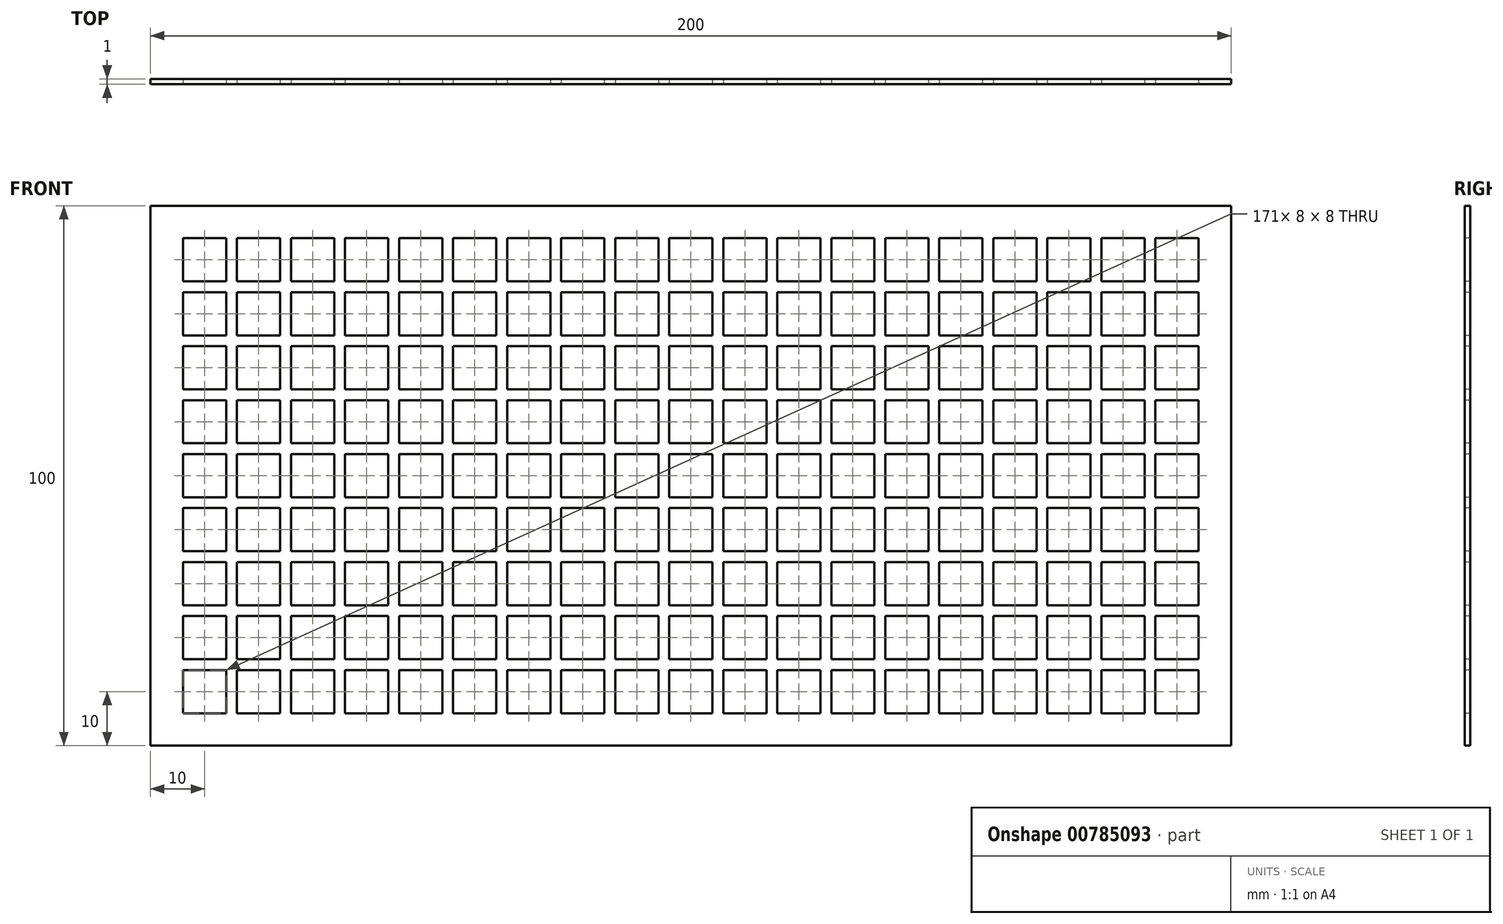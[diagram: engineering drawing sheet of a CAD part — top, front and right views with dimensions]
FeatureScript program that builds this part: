
annotation { "Feature Type Name" : "Feature", "Feature Type Description" : "" }
export const myFeature = defineFeature(function(context is Context, id is Id, definition is map)
    precondition{}
    {
        {
            var Q0;
            Q0=qCreatedBy(makeId("Front.planeOp"),FACE);
            var sketch = newSketch(context, id + "F0", { "sketchPlane" : qUnion([Q0])});
            skLineSegment(sketch, "E0.bottom", {"start": v(0, 0) * mm, "end": v(200, 0) * mm});
            skLineSegment(sketch, "E0.top", {"start": v(0, 100) * mm, "end": v(200, 100) * mm});
            skLineSegment(sketch, "E0.left", {"start": v(0, 0) * mm, "end": v(0, 100) * mm});
            skLineSegment(sketch, "E0.right", {"start": v(200, 0) * mm, "end": v(200, 100) * mm});
            skSolve(sketch);
        }
        {
            var Q0;
            Q0=makeQuery(id+"F0.imprint","IMPRINT",FACE,{"disambiguationData":[TD([[makeQuery(id+"F0.imprint","IMPRINT",EDGE,{"derivedFrom":sQuery(id+"F0.wireOp",EDGE,"E0.bottom")}),1.0]])]});
            extrude(context, id + "F1", {"entities" : qUnion([Q0]), "depth" : 1 * mm, "offsetDistance" : 25 * mm});
        }
        {
            var Q0;
            Q0=makeQuery(id+"F1.opExtrude","CAP_FACE",FACE,{"disambiguationData":[OSD([sQuery(id+"F0.wireOp",EDGE,"E0.bottom"),sQuery(id+"F0.wireOp",EDGE,"E0.top"),sQuery(id+"F0.wireOp",EDGE,"E0.left"),sQuery(id+"F0.wireOp",EDGE,"E0.right")])],"isStart":false});
            var sketch = newSketch(context, id + "F2", { "sketchPlane" : qUnion([Q0])});
            skLineSegment(sketch, "E1.bottom", {"start": v(6, 94) * mm, "end": v(14, 94) * mm});
            skLineSegment(sketch, "E1.top", {"start": v(6, 86) * mm, "end": v(14, 86) * mm});
            skLineSegment(sketch, "E1.left", {"start": v(6, 94) * mm, "end": v(6, 86) * mm});
            skLineSegment(sketch, "E1.right", {"start": v(14, 94) * mm, "end": v(14, 86) * mm});
            skLineSegment(sketch, "E2.0.1.0", {"start": v(14, 84) * mm, "end": v(14, 76) * mm});
            skLineSegment(sketch, "E2.0.1.1", {"start": v(6, 84) * mm, "end": v(6, 76) * mm});
            skLineSegment(sketch, "E2.0.1.2", {"start": v(6, 76) * mm, "end": v(14, 76) * mm});
            skLineSegment(sketch, "E2.0.1.3", {"start": v(6, 84) * mm, "end": v(14, 84) * mm});
            skLineSegment(sketch, "E2.0.2.0", {"start": v(14, 74) * mm, "end": v(14, 66) * mm});
            skLineSegment(sketch, "E2.0.2.1", {"start": v(6, 74) * mm, "end": v(6, 66) * mm});
            skLineSegment(sketch, "E2.0.2.2", {"start": v(6, 66) * mm, "end": v(14, 66) * mm});
            skLineSegment(sketch, "E2.0.2.3", {"start": v(6, 74) * mm, "end": v(14, 74) * mm});
            skLineSegment(sketch, "E2.0.3.0", {"start": v(14, 64) * mm, "end": v(14, 56) * mm});
            skLineSegment(sketch, "E2.0.3.1", {"start": v(6, 64) * mm, "end": v(6, 56) * mm});
            skLineSegment(sketch, "E2.0.3.2", {"start": v(6, 56) * mm, "end": v(14, 56) * mm});
            skLineSegment(sketch, "E2.0.3.3", {"start": v(6, 64) * mm, "end": v(14, 64) * mm});
            skLineSegment(sketch, "E2.0.4.0", {"start": v(14, 54) * mm, "end": v(14, 46) * mm});
            skLineSegment(sketch, "E2.0.4.1", {"start": v(6, 54) * mm, "end": v(6, 46) * mm});
            skLineSegment(sketch, "E2.0.4.2", {"start": v(6, 46) * mm, "end": v(14, 46) * mm});
            skLineSegment(sketch, "E2.0.4.3", {"start": v(6, 54) * mm, "end": v(14, 54) * mm});
            skLineSegment(sketch, "E2.0.5.0", {"start": v(14, 44) * mm, "end": v(14, 36) * mm});
            skLineSegment(sketch, "E2.0.5.1", {"start": v(6, 44) * mm, "end": v(6, 36) * mm});
            skLineSegment(sketch, "E2.0.5.2", {"start": v(6, 36) * mm, "end": v(14, 36) * mm});
            skLineSegment(sketch, "E2.0.5.3", {"start": v(6, 44) * mm, "end": v(14, 44) * mm});
            skLineSegment(sketch, "E2.0.6.0", {"start": v(14, 34) * mm, "end": v(14, 26) * mm});
            skLineSegment(sketch, "E2.0.6.1", {"start": v(6, 34) * mm, "end": v(6, 26) * mm});
            skLineSegment(sketch, "E2.0.6.2", {"start": v(6, 26) * mm, "end": v(14, 26) * mm});
            skLineSegment(sketch, "E2.0.6.3", {"start": v(6, 34) * mm, "end": v(14, 34) * mm});
            skLineSegment(sketch, "E2.0.7.0", {"start": v(14, 24) * mm, "end": v(14, 16) * mm});
            skLineSegment(sketch, "E2.0.7.1", {"start": v(6, 24) * mm, "end": v(6, 16) * mm});
            skLineSegment(sketch, "E2.0.7.2", {"start": v(6, 16) * mm, "end": v(14, 16) * mm});
            skLineSegment(sketch, "E2.0.7.3", {"start": v(6, 24) * mm, "end": v(14, 24) * mm});
            skLineSegment(sketch, "E2.0.8.0", {"start": v(14, 14) * mm, "end": v(14, 6) * mm});
            skLineSegment(sketch, "E2.0.8.1", {"start": v(6, 14) * mm, "end": v(6, 6) * mm});
            skLineSegment(sketch, "E2.0.8.2", {"start": v(6, 6) * mm, "end": v(14, 6) * mm});
            skLineSegment(sketch, "E2.0.8.3", {"start": v(6, 14) * mm, "end": v(14, 14) * mm});
            skLineSegment(sketch, "E2.1.0.0", {"start": v(24, 94) * mm, "end": v(24, 86) * mm});
            skLineSegment(sketch, "E2.1.0.1", {"start": v(16, 94) * mm, "end": v(16, 86) * mm});
            skLineSegment(sketch, "E2.1.0.2", {"start": v(16, 86) * mm, "end": v(24, 86) * mm});
            skLineSegment(sketch, "E2.1.0.3", {"start": v(16, 94) * mm, "end": v(24, 94) * mm});
            skLineSegment(sketch, "E2.1.1.0", {"start": v(24, 84) * mm, "end": v(24, 76) * mm});
            skLineSegment(sketch, "E2.1.1.1", {"start": v(16, 84) * mm, "end": v(16, 76) * mm});
            skLineSegment(sketch, "E2.1.1.2", {"start": v(16, 76) * mm, "end": v(24, 76) * mm});
            skLineSegment(sketch, "E2.1.1.3", {"start": v(16, 84) * mm, "end": v(24, 84) * mm});
            skLineSegment(sketch, "E2.1.2.0", {"start": v(24, 74) * mm, "end": v(24, 66) * mm});
            skLineSegment(sketch, "E2.1.2.1", {"start": v(16, 74) * mm, "end": v(16, 66) * mm});
            skLineSegment(sketch, "E2.1.2.2", {"start": v(16, 66) * mm, "end": v(24, 66) * mm});
            skLineSegment(sketch, "E2.1.2.3", {"start": v(16, 74) * mm, "end": v(24, 74) * mm});
            skLineSegment(sketch, "E2.1.3.0", {"start": v(24, 64) * mm, "end": v(24, 56) * mm});
            skLineSegment(sketch, "E2.1.3.1", {"start": v(16, 64) * mm, "end": v(16, 56) * mm});
            skLineSegment(sketch, "E2.1.3.2", {"start": v(16, 56) * mm, "end": v(24, 56) * mm});
            skLineSegment(sketch, "E2.1.3.3", {"start": v(16, 64) * mm, "end": v(24, 64) * mm});
            skLineSegment(sketch, "E2.1.4.0", {"start": v(24, 54) * mm, "end": v(24, 46) * mm});
            skLineSegment(sketch, "E2.1.4.1", {"start": v(16, 54) * mm, "end": v(16, 46) * mm});
            skLineSegment(sketch, "E2.1.4.2", {"start": v(16, 46) * mm, "end": v(24, 46) * mm});
            skLineSegment(sketch, "E2.1.4.3", {"start": v(16, 54) * mm, "end": v(24, 54) * mm});
            skLineSegment(sketch, "E2.1.5.0", {"start": v(24, 44) * mm, "end": v(24, 36) * mm});
            skLineSegment(sketch, "E2.1.5.1", {"start": v(16, 44) * mm, "end": v(16, 36) * mm});
            skLineSegment(sketch, "E2.1.5.2", {"start": v(16, 36) * mm, "end": v(24, 36) * mm});
            skLineSegment(sketch, "E2.1.5.3", {"start": v(16, 44) * mm, "end": v(24, 44) * mm});
            skLineSegment(sketch, "E2.1.6.0", {"start": v(24, 34) * mm, "end": v(24, 26) * mm});
            skLineSegment(sketch, "E2.1.6.1", {"start": v(16, 34) * mm, "end": v(16, 26) * mm});
            skLineSegment(sketch, "E2.1.6.2", {"start": v(16, 26) * mm, "end": v(24, 26) * mm});
            skLineSegment(sketch, "E2.1.6.3", {"start": v(16, 34) * mm, "end": v(24, 34) * mm});
            skLineSegment(sketch, "E2.1.7.0", {"start": v(24, 24) * mm, "end": v(24, 16) * mm});
            skLineSegment(sketch, "E2.1.7.1", {"start": v(16, 24) * mm, "end": v(16, 16) * mm});
            skLineSegment(sketch, "E2.1.7.2", {"start": v(16, 16) * mm, "end": v(24, 16) * mm});
            skLineSegment(sketch, "E2.1.7.3", {"start": v(16, 24) * mm, "end": v(24, 24) * mm});
            skLineSegment(sketch, "E2.1.8.0", {"start": v(24, 14) * mm, "end": v(24, 6) * mm});
            skLineSegment(sketch, "E2.1.8.1", {"start": v(16, 14) * mm, "end": v(16, 6) * mm});
            skLineSegment(sketch, "E2.1.8.2", {"start": v(16, 6) * mm, "end": v(24, 6) * mm});
            skLineSegment(sketch, "E2.1.8.3", {"start": v(16, 14) * mm, "end": v(24, 14) * mm});
            skLineSegment(sketch, "E2.2.0.0", {"start": v(34, 94) * mm, "end": v(34, 86) * mm});
            skLineSegment(sketch, "E2.2.0.1", {"start": v(26, 94) * mm, "end": v(26, 86) * mm});
            skLineSegment(sketch, "E2.2.0.2", {"start": v(26, 86) * mm, "end": v(34, 86) * mm});
            skLineSegment(sketch, "E2.2.0.3", {"start": v(26, 94) * mm, "end": v(34, 94) * mm});
            skLineSegment(sketch, "E2.2.1.0", {"start": v(34, 84) * mm, "end": v(34, 76) * mm});
            skLineSegment(sketch, "E2.2.1.1", {"start": v(26, 84) * mm, "end": v(26, 76) * mm});
            skLineSegment(sketch, "E2.2.1.2", {"start": v(26, 76) * mm, "end": v(34, 76) * mm});
            skLineSegment(sketch, "E2.2.1.3", {"start": v(26, 84) * mm, "end": v(34, 84) * mm});
            skLineSegment(sketch, "E2.2.2.0", {"start": v(34, 74) * mm, "end": v(34, 66) * mm});
            skLineSegment(sketch, "E2.2.2.1", {"start": v(26, 74) * mm, "end": v(26, 66) * mm});
            skLineSegment(sketch, "E2.2.2.2", {"start": v(26, 66) * mm, "end": v(34, 66) * mm});
            skLineSegment(sketch, "E2.2.2.3", {"start": v(26, 74) * mm, "end": v(34, 74) * mm});
            skLineSegment(sketch, "E2.2.3.0", {"start": v(34, 64) * mm, "end": v(34, 56) * mm});
            skLineSegment(sketch, "E2.2.3.1", {"start": v(26, 64) * mm, "end": v(26, 56) * mm});
            skLineSegment(sketch, "E2.2.3.2", {"start": v(26, 56) * mm, "end": v(34, 56) * mm});
            skLineSegment(sketch, "E2.2.3.3", {"start": v(26, 64) * mm, "end": v(34, 64) * mm});
            skLineSegment(sketch, "E2.2.4.0", {"start": v(34, 54) * mm, "end": v(34, 46) * mm});
            skLineSegment(sketch, "E2.2.4.1", {"start": v(26, 54) * mm, "end": v(26, 46) * mm});
            skLineSegment(sketch, "E2.2.4.2", {"start": v(26, 46) * mm, "end": v(34, 46) * mm});
            skLineSegment(sketch, "E2.2.4.3", {"start": v(26, 54) * mm, "end": v(34, 54) * mm});
            skLineSegment(sketch, "E2.2.5.0", {"start": v(34, 44) * mm, "end": v(34, 36) * mm});
            skLineSegment(sketch, "E2.2.5.1", {"start": v(26, 44) * mm, "end": v(26, 36) * mm});
            skLineSegment(sketch, "E2.2.5.2", {"start": v(26, 36) * mm, "end": v(34, 36) * mm});
            skLineSegment(sketch, "E2.2.5.3", {"start": v(26, 44) * mm, "end": v(34, 44) * mm});
            skLineSegment(sketch, "E2.2.6.0", {"start": v(34, 34) * mm, "end": v(34, 26) * mm});
            skLineSegment(sketch, "E2.2.6.1", {"start": v(26, 34) * mm, "end": v(26, 26) * mm});
            skLineSegment(sketch, "E2.2.6.2", {"start": v(26, 26) * mm, "end": v(34, 26) * mm});
            skLineSegment(sketch, "E2.2.6.3", {"start": v(26, 34) * mm, "end": v(34, 34) * mm});
            skLineSegment(sketch, "E2.2.7.0", {"start": v(34, 24) * mm, "end": v(34, 16) * mm});
            skLineSegment(sketch, "E2.2.7.1", {"start": v(26, 24) * mm, "end": v(26, 16) * mm});
            skLineSegment(sketch, "E2.2.7.2", {"start": v(26, 16) * mm, "end": v(34, 16) * mm});
            skLineSegment(sketch, "E2.2.7.3", {"start": v(26, 24) * mm, "end": v(34, 24) * mm});
            skLineSegment(sketch, "E2.2.8.0", {"start": v(34, 14) * mm, "end": v(34, 6) * mm});
            skLineSegment(sketch, "E2.2.8.1", {"start": v(26, 14) * mm, "end": v(26, 6) * mm});
            skLineSegment(sketch, "E2.2.8.2", {"start": v(26, 6) * mm, "end": v(34, 6) * mm});
            skLineSegment(sketch, "E2.2.8.3", {"start": v(26, 14) * mm, "end": v(34, 14) * mm});
            skLineSegment(sketch, "E2.3.0.0", {"start": v(44, 94) * mm, "end": v(44, 86) * mm});
            skLineSegment(sketch, "E2.3.0.1", {"start": v(36, 94) * mm, "end": v(36, 86) * mm});
            skLineSegment(sketch, "E2.3.0.2", {"start": v(36, 86) * mm, "end": v(44, 86) * mm});
            skLineSegment(sketch, "E2.3.0.3", {"start": v(36, 94) * mm, "end": v(44, 94) * mm});
            skLineSegment(sketch, "E2.3.1.0", {"start": v(44, 84) * mm, "end": v(44, 76) * mm});
            skLineSegment(sketch, "E2.3.1.1", {"start": v(36, 84) * mm, "end": v(36, 76) * mm});
            skLineSegment(sketch, "E2.3.1.2", {"start": v(36, 76) * mm, "end": v(44, 76) * mm});
            skLineSegment(sketch, "E2.3.1.3", {"start": v(36, 84) * mm, "end": v(44, 84) * mm});
            skLineSegment(sketch, "E2.3.2.0", {"start": v(44, 74) * mm, "end": v(44, 66) * mm});
            skLineSegment(sketch, "E2.3.2.1", {"start": v(36, 74) * mm, "end": v(36, 66) * mm});
            skLineSegment(sketch, "E2.3.2.2", {"start": v(36, 66) * mm, "end": v(44, 66) * mm});
            skLineSegment(sketch, "E2.3.2.3", {"start": v(36, 74) * mm, "end": v(44, 74) * mm});
            skLineSegment(sketch, "E2.3.3.0", {"start": v(44, 64) * mm, "end": v(44, 56) * mm});
            skLineSegment(sketch, "E2.3.3.1", {"start": v(36, 64) * mm, "end": v(36, 56) * mm});
            skLineSegment(sketch, "E2.3.3.2", {"start": v(36, 56) * mm, "end": v(44, 56) * mm});
            skLineSegment(sketch, "E2.3.3.3", {"start": v(36, 64) * mm, "end": v(44, 64) * mm});
            skLineSegment(sketch, "E2.3.4.0", {"start": v(44, 54) * mm, "end": v(44, 46) * mm});
            skLineSegment(sketch, "E2.3.4.1", {"start": v(36, 54) * mm, "end": v(36, 46) * mm});
            skLineSegment(sketch, "E2.3.4.2", {"start": v(36, 46) * mm, "end": v(44, 46) * mm});
            skLineSegment(sketch, "E2.3.4.3", {"start": v(36, 54) * mm, "end": v(44, 54) * mm});
            skLineSegment(sketch, "E2.3.5.0", {"start": v(44, 44) * mm, "end": v(44, 36) * mm});
            skLineSegment(sketch, "E2.3.5.1", {"start": v(36, 44) * mm, "end": v(36, 36) * mm});
            skLineSegment(sketch, "E2.3.5.2", {"start": v(36, 36) * mm, "end": v(44, 36) * mm});
            skLineSegment(sketch, "E2.3.5.3", {"start": v(36, 44) * mm, "end": v(44, 44) * mm});
            skLineSegment(sketch, "E2.3.6.0", {"start": v(44, 34) * mm, "end": v(44, 26) * mm});
            skLineSegment(sketch, "E2.3.6.1", {"start": v(36, 34) * mm, "end": v(36, 26) * mm});
            skLineSegment(sketch, "E2.3.6.2", {"start": v(36, 26) * mm, "end": v(44, 26) * mm});
            skLineSegment(sketch, "E2.3.6.3", {"start": v(36, 34) * mm, "end": v(44, 34) * mm});
            skLineSegment(sketch, "E2.3.7.0", {"start": v(44, 24) * mm, "end": v(44, 16) * mm});
            skLineSegment(sketch, "E2.3.7.1", {"start": v(36, 24) * mm, "end": v(36, 16) * mm});
            skLineSegment(sketch, "E2.3.7.2", {"start": v(36, 16) * mm, "end": v(44, 16) * mm});
            skLineSegment(sketch, "E2.3.7.3", {"start": v(36, 24) * mm, "end": v(44, 24) * mm});
            skLineSegment(sketch, "E2.3.8.0", {"start": v(44, 14) * mm, "end": v(44, 6) * mm});
            skLineSegment(sketch, "E2.3.8.1", {"start": v(36, 14) * mm, "end": v(36, 6) * mm});
            skLineSegment(sketch, "E2.3.8.2", {"start": v(36, 6) * mm, "end": v(44, 6) * mm});
            skLineSegment(sketch, "E2.3.8.3", {"start": v(36, 14) * mm, "end": v(44, 14) * mm});
            skLineSegment(sketch, "E2.4.0.0", {"start": v(54, 94) * mm, "end": v(54, 86) * mm});
            skLineSegment(sketch, "E2.4.0.1", {"start": v(46, 94) * mm, "end": v(46, 86) * mm});
            skLineSegment(sketch, "E2.4.0.2", {"start": v(46, 86) * mm, "end": v(54, 86) * mm});
            skLineSegment(sketch, "E2.4.0.3", {"start": v(46, 94) * mm, "end": v(54, 94) * mm});
            skLineSegment(sketch, "E2.4.1.0", {"start": v(54, 84) * mm, "end": v(54, 76) * mm});
            skLineSegment(sketch, "E2.4.1.1", {"start": v(46, 84) * mm, "end": v(46, 76) * mm});
            skLineSegment(sketch, "E2.4.1.2", {"start": v(46, 76) * mm, "end": v(54, 76) * mm});
            skLineSegment(sketch, "E2.4.1.3", {"start": v(46, 84) * mm, "end": v(54, 84) * mm});
            skLineSegment(sketch, "E2.4.2.0", {"start": v(54, 74) * mm, "end": v(54, 66) * mm});
            skLineSegment(sketch, "E2.4.2.1", {"start": v(46, 74) * mm, "end": v(46, 66) * mm});
            skLineSegment(sketch, "E2.4.2.2", {"start": v(46, 66) * mm, "end": v(54, 66) * mm});
            skLineSegment(sketch, "E2.4.2.3", {"start": v(46, 74) * mm, "end": v(54, 74) * mm});
            skLineSegment(sketch, "E2.4.3.0", {"start": v(54, 64) * mm, "end": v(54, 56) * mm});
            skLineSegment(sketch, "E2.4.3.1", {"start": v(46, 64) * mm, "end": v(46, 56) * mm});
            skLineSegment(sketch, "E2.4.3.2", {"start": v(46, 56) * mm, "end": v(54, 56) * mm});
            skLineSegment(sketch, "E2.4.3.3", {"start": v(46, 64) * mm, "end": v(54, 64) * mm});
            skLineSegment(sketch, "E2.4.4.0", {"start": v(54, 54) * mm, "end": v(54, 46) * mm});
            skLineSegment(sketch, "E2.4.4.1", {"start": v(46, 54) * mm, "end": v(46, 46) * mm});
            skLineSegment(sketch, "E2.4.4.2", {"start": v(46, 46) * mm, "end": v(54, 46) * mm});
            skLineSegment(sketch, "E2.4.4.3", {"start": v(46, 54) * mm, "end": v(54, 54) * mm});
            skLineSegment(sketch, "E2.4.5.0", {"start": v(54, 44) * mm, "end": v(54, 36) * mm});
            skLineSegment(sketch, "E2.4.5.1", {"start": v(46, 44) * mm, "end": v(46, 36) * mm});
            skLineSegment(sketch, "E2.4.5.2", {"start": v(46, 36) * mm, "end": v(54, 36) * mm});
            skLineSegment(sketch, "E2.4.5.3", {"start": v(46, 44) * mm, "end": v(54, 44) * mm});
            skLineSegment(sketch, "E2.4.6.0", {"start": v(54, 34) * mm, "end": v(54, 26) * mm});
            skLineSegment(sketch, "E2.4.6.1", {"start": v(46, 34) * mm, "end": v(46, 26) * mm});
            skLineSegment(sketch, "E2.4.6.2", {"start": v(46, 26) * mm, "end": v(54, 26) * mm});
            skLineSegment(sketch, "E2.4.6.3", {"start": v(46, 34) * mm, "end": v(54, 34) * mm});
            skLineSegment(sketch, "E2.4.7.0", {"start": v(54, 24) * mm, "end": v(54, 16) * mm});
            skLineSegment(sketch, "E2.4.7.1", {"start": v(46, 24) * mm, "end": v(46, 16) * mm});
            skLineSegment(sketch, "E2.4.7.2", {"start": v(46, 16) * mm, "end": v(54, 16) * mm});
            skLineSegment(sketch, "E2.4.7.3", {"start": v(46, 24) * mm, "end": v(54, 24) * mm});
            skLineSegment(sketch, "E2.4.8.0", {"start": v(54, 14) * mm, "end": v(54, 6) * mm});
            skLineSegment(sketch, "E2.4.8.1", {"start": v(46, 14) * mm, "end": v(46, 6) * mm});
            skLineSegment(sketch, "E2.4.8.2", {"start": v(46, 6) * mm, "end": v(54, 6) * mm});
            skLineSegment(sketch, "E2.4.8.3", {"start": v(46, 14) * mm, "end": v(54, 14) * mm});
            skLineSegment(sketch, "E2.5.0.0", {"start": v(64, 94) * mm, "end": v(64, 86) * mm});
            skLineSegment(sketch, "E2.5.0.1", {"start": v(56, 94) * mm, "end": v(56, 86) * mm});
            skLineSegment(sketch, "E2.5.0.2", {"start": v(56, 86) * mm, "end": v(64, 86) * mm});
            skLineSegment(sketch, "E2.5.0.3", {"start": v(56, 94) * mm, "end": v(64, 94) * mm});
            skLineSegment(sketch, "E2.5.1.0", {"start": v(64, 84) * mm, "end": v(64, 76) * mm});
            skLineSegment(sketch, "E2.5.1.1", {"start": v(56, 84) * mm, "end": v(56, 76) * mm});
            skLineSegment(sketch, "E2.5.1.2", {"start": v(56, 76) * mm, "end": v(64, 76) * mm});
            skLineSegment(sketch, "E2.5.1.3", {"start": v(56, 84) * mm, "end": v(64, 84) * mm});
            skLineSegment(sketch, "E2.5.2.0", {"start": v(64, 74) * mm, "end": v(64, 66) * mm});
            skLineSegment(sketch, "E2.5.2.1", {"start": v(56, 74) * mm, "end": v(56, 66) * mm});
            skLineSegment(sketch, "E2.5.2.2", {"start": v(56, 66) * mm, "end": v(64, 66) * mm});
            skLineSegment(sketch, "E2.5.2.3", {"start": v(56, 74) * mm, "end": v(64, 74) * mm});
            skLineSegment(sketch, "E2.5.3.0", {"start": v(64, 64) * mm, "end": v(64, 56) * mm});
            skLineSegment(sketch, "E2.5.3.1", {"start": v(56, 64) * mm, "end": v(56, 56) * mm});
            skLineSegment(sketch, "E2.5.3.2", {"start": v(56, 56) * mm, "end": v(64, 56) * mm});
            skLineSegment(sketch, "E2.5.3.3", {"start": v(56, 64) * mm, "end": v(64, 64) * mm});
            skLineSegment(sketch, "E2.5.4.0", {"start": v(64, 54) * mm, "end": v(64, 46) * mm});
            skLineSegment(sketch, "E2.5.4.1", {"start": v(56, 54) * mm, "end": v(56, 46) * mm});
            skLineSegment(sketch, "E2.5.4.2", {"start": v(56, 46) * mm, "end": v(64, 46) * mm});
            skLineSegment(sketch, "E2.5.4.3", {"start": v(56, 54) * mm, "end": v(64, 54) * mm});
            skLineSegment(sketch, "E2.5.5.0", {"start": v(64, 44) * mm, "end": v(64, 36) * mm});
            skLineSegment(sketch, "E2.5.5.1", {"start": v(56, 44) * mm, "end": v(56, 36) * mm});
            skLineSegment(sketch, "E2.5.5.2", {"start": v(56, 36) * mm, "end": v(64, 36) * mm});
            skLineSegment(sketch, "E2.5.5.3", {"start": v(56, 44) * mm, "end": v(64, 44) * mm});
            skLineSegment(sketch, "E2.5.6.0", {"start": v(64, 34) * mm, "end": v(64, 26) * mm});
            skLineSegment(sketch, "E2.5.6.1", {"start": v(56, 34) * mm, "end": v(56, 26) * mm});
            skLineSegment(sketch, "E2.5.6.2", {"start": v(56, 26) * mm, "end": v(64, 26) * mm});
            skLineSegment(sketch, "E2.5.6.3", {"start": v(56, 34) * mm, "end": v(64, 34) * mm});
            skLineSegment(sketch, "E2.5.7.0", {"start": v(64, 24) * mm, "end": v(64, 16) * mm});
            skLineSegment(sketch, "E2.5.7.1", {"start": v(56, 24) * mm, "end": v(56, 16) * mm});
            skLineSegment(sketch, "E2.5.7.2", {"start": v(56, 16) * mm, "end": v(64, 16) * mm});
            skLineSegment(sketch, "E2.5.7.3", {"start": v(56, 24) * mm, "end": v(64, 24) * mm});
            skLineSegment(sketch, "E2.5.8.0", {"start": v(64, 14) * mm, "end": v(64, 6) * mm});
            skLineSegment(sketch, "E2.5.8.1", {"start": v(56, 14) * mm, "end": v(56, 6) * mm});
            skLineSegment(sketch, "E2.5.8.2", {"start": v(56, 6) * mm, "end": v(64, 6) * mm});
            skLineSegment(sketch, "E2.5.8.3", {"start": v(56, 14) * mm, "end": v(64, 14) * mm});
            skLineSegment(sketch, "E2.6.0.0", {"start": v(74, 94) * mm, "end": v(74, 86) * mm});
            skLineSegment(sketch, "E2.6.0.1", {"start": v(66, 94) * mm, "end": v(66, 86) * mm});
            skLineSegment(sketch, "E2.6.0.2", {"start": v(66, 86) * mm, "end": v(74, 86) * mm});
            skLineSegment(sketch, "E2.6.0.3", {"start": v(66, 94) * mm, "end": v(74, 94) * mm});
            skLineSegment(sketch, "E2.6.1.0", {"start": v(74, 84) * mm, "end": v(74, 76) * mm});
            skLineSegment(sketch, "E2.6.1.1", {"start": v(66, 84) * mm, "end": v(66, 76) * mm});
            skLineSegment(sketch, "E2.6.1.2", {"start": v(66, 76) * mm, "end": v(74, 76) * mm});
            skLineSegment(sketch, "E2.6.1.3", {"start": v(66, 84) * mm, "end": v(74, 84) * mm});
            skLineSegment(sketch, "E2.6.2.0", {"start": v(74, 74) * mm, "end": v(74, 66) * mm});
            skLineSegment(sketch, "E2.6.2.1", {"start": v(66, 74) * mm, "end": v(66, 66) * mm});
            skLineSegment(sketch, "E2.6.2.2", {"start": v(66, 66) * mm, "end": v(74, 66) * mm});
            skLineSegment(sketch, "E2.6.2.3", {"start": v(66, 74) * mm, "end": v(74, 74) * mm});
            skLineSegment(sketch, "E2.6.3.0", {"start": v(74, 64) * mm, "end": v(74, 56) * mm});
            skLineSegment(sketch, "E2.6.3.1", {"start": v(66, 64) * mm, "end": v(66, 56) * mm});
            skLineSegment(sketch, "E2.6.3.2", {"start": v(66, 56) * mm, "end": v(74, 56) * mm});
            skLineSegment(sketch, "E2.6.3.3", {"start": v(66, 64) * mm, "end": v(74, 64) * mm});
            skLineSegment(sketch, "E2.6.4.0", {"start": v(74, 54) * mm, "end": v(74, 46) * mm});
            skLineSegment(sketch, "E2.6.4.1", {"start": v(66, 54) * mm, "end": v(66, 46) * mm});
            skLineSegment(sketch, "E2.6.4.2", {"start": v(66, 46) * mm, "end": v(74, 46) * mm});
            skLineSegment(sketch, "E2.6.4.3", {"start": v(66, 54) * mm, "end": v(74, 54) * mm});
            skLineSegment(sketch, "E2.6.5.0", {"start": v(74, 44) * mm, "end": v(74, 36) * mm});
            skLineSegment(sketch, "E2.6.5.1", {"start": v(66, 44) * mm, "end": v(66, 36) * mm});
            skLineSegment(sketch, "E2.6.5.2", {"start": v(66, 36) * mm, "end": v(74, 36) * mm});
            skLineSegment(sketch, "E2.6.5.3", {"start": v(66, 44) * mm, "end": v(74, 44) * mm});
            skLineSegment(sketch, "E2.6.6.0", {"start": v(74, 34) * mm, "end": v(74, 26) * mm});
            skLineSegment(sketch, "E2.6.6.1", {"start": v(66, 34) * mm, "end": v(66, 26) * mm});
            skLineSegment(sketch, "E2.6.6.2", {"start": v(66, 26) * mm, "end": v(74, 26) * mm});
            skLineSegment(sketch, "E2.6.6.3", {"start": v(66, 34) * mm, "end": v(74, 34) * mm});
            skLineSegment(sketch, "E2.6.7.0", {"start": v(74, 24) * mm, "end": v(74, 16) * mm});
            skLineSegment(sketch, "E2.6.7.1", {"start": v(66, 24) * mm, "end": v(66, 16) * mm});
            skLineSegment(sketch, "E2.6.7.2", {"start": v(66, 16) * mm, "end": v(74, 16) * mm});
            skLineSegment(sketch, "E2.6.7.3", {"start": v(66, 24) * mm, "end": v(74, 24) * mm});
            skLineSegment(sketch, "E2.6.8.0", {"start": v(74, 14) * mm, "end": v(74, 6) * mm});
            skLineSegment(sketch, "E2.6.8.1", {"start": v(66, 14) * mm, "end": v(66, 6) * mm});
            skLineSegment(sketch, "E2.6.8.2", {"start": v(66, 6) * mm, "end": v(74, 6) * mm});
            skLineSegment(sketch, "E2.6.8.3", {"start": v(66, 14) * mm, "end": v(74, 14) * mm});
            skLineSegment(sketch, "E2.7.0.0", {"start": v(84, 94) * mm, "end": v(84, 86) * mm});
            skLineSegment(sketch, "E2.7.0.1", {"start": v(76, 94) * mm, "end": v(76, 86) * mm});
            skLineSegment(sketch, "E2.7.0.2", {"start": v(76, 86) * mm, "end": v(84, 86) * mm});
            skLineSegment(sketch, "E2.7.0.3", {"start": v(76, 94) * mm, "end": v(84, 94) * mm});
            skLineSegment(sketch, "E2.7.1.0", {"start": v(84, 84) * mm, "end": v(84, 76) * mm});
            skLineSegment(sketch, "E2.7.1.1", {"start": v(76, 84) * mm, "end": v(76, 76) * mm});
            skLineSegment(sketch, "E2.7.1.2", {"start": v(76, 76) * mm, "end": v(84, 76) * mm});
            skLineSegment(sketch, "E2.7.1.3", {"start": v(76, 84) * mm, "end": v(84, 84) * mm});
            skLineSegment(sketch, "E2.7.2.0", {"start": v(84, 74) * mm, "end": v(84, 66) * mm});
            skLineSegment(sketch, "E2.7.2.1", {"start": v(76, 74) * mm, "end": v(76, 66) * mm});
            skLineSegment(sketch, "E2.7.2.2", {"start": v(76, 66) * mm, "end": v(84, 66) * mm});
            skLineSegment(sketch, "E2.7.2.3", {"start": v(76, 74) * mm, "end": v(84, 74) * mm});
            skLineSegment(sketch, "E2.7.3.0", {"start": v(84, 64) * mm, "end": v(84, 56) * mm});
            skLineSegment(sketch, "E2.7.3.1", {"start": v(76, 64) * mm, "end": v(76, 56) * mm});
            skLineSegment(sketch, "E2.7.3.2", {"start": v(76, 56) * mm, "end": v(84, 56) * mm});
            skLineSegment(sketch, "E2.7.3.3", {"start": v(76, 64) * mm, "end": v(84, 64) * mm});
            skLineSegment(sketch, "E2.7.4.0", {"start": v(84, 54) * mm, "end": v(84, 46) * mm});
            skLineSegment(sketch, "E2.7.4.1", {"start": v(76, 54) * mm, "end": v(76, 46) * mm});
            skLineSegment(sketch, "E2.7.4.2", {"start": v(76, 46) * mm, "end": v(84, 46) * mm});
            skLineSegment(sketch, "E2.7.4.3", {"start": v(76, 54) * mm, "end": v(84, 54) * mm});
            skLineSegment(sketch, "E2.7.5.0", {"start": v(84, 44) * mm, "end": v(84, 36) * mm});
            skLineSegment(sketch, "E2.7.5.1", {"start": v(76, 44) * mm, "end": v(76, 36) * mm});
            skLineSegment(sketch, "E2.7.5.2", {"start": v(76, 36) * mm, "end": v(84, 36) * mm});
            skLineSegment(sketch, "E2.7.5.3", {"start": v(76, 44) * mm, "end": v(84, 44) * mm});
            skLineSegment(sketch, "E2.7.6.0", {"start": v(84, 34) * mm, "end": v(84, 26) * mm});
            skLineSegment(sketch, "E2.7.6.1", {"start": v(76, 34) * mm, "end": v(76, 26) * mm});
            skLineSegment(sketch, "E2.7.6.2", {"start": v(76, 26) * mm, "end": v(84, 26) * mm});
            skLineSegment(sketch, "E2.7.6.3", {"start": v(76, 34) * mm, "end": v(84, 34) * mm});
            skLineSegment(sketch, "E2.7.7.0", {"start": v(84, 24) * mm, "end": v(84, 16) * mm});
            skLineSegment(sketch, "E2.7.7.1", {"start": v(76, 24) * mm, "end": v(76, 16) * mm});
            skLineSegment(sketch, "E2.7.7.2", {"start": v(76, 16) * mm, "end": v(84, 16) * mm});
            skLineSegment(sketch, "E2.7.7.3", {"start": v(76, 24) * mm, "end": v(84, 24) * mm});
            skLineSegment(sketch, "E2.7.8.0", {"start": v(84, 14) * mm, "end": v(84, 6) * mm});
            skLineSegment(sketch, "E2.7.8.1", {"start": v(76, 14) * mm, "end": v(76, 6) * mm});
            skLineSegment(sketch, "E2.7.8.2", {"start": v(76, 6) * mm, "end": v(84, 6) * mm});
            skLineSegment(sketch, "E2.7.8.3", {"start": v(76, 14) * mm, "end": v(84, 14) * mm});
            skLineSegment(sketch, "E2.8.0.0", {"start": v(94, 94) * mm, "end": v(94, 86) * mm});
            skLineSegment(sketch, "E2.8.0.1", {"start": v(86, 94) * mm, "end": v(86, 86) * mm});
            skLineSegment(sketch, "E2.8.0.2", {"start": v(86, 86) * mm, "end": v(94, 86) * mm});
            skLineSegment(sketch, "E2.8.0.3", {"start": v(86, 94) * mm, "end": v(94, 94) * mm});
            skLineSegment(sketch, "E2.8.1.0", {"start": v(94, 84) * mm, "end": v(94, 76) * mm});
            skLineSegment(sketch, "E2.8.1.1", {"start": v(86, 84) * mm, "end": v(86, 76) * mm});
            skLineSegment(sketch, "E2.8.1.2", {"start": v(86, 76) * mm, "end": v(94, 76) * mm});
            skLineSegment(sketch, "E2.8.1.3", {"start": v(86, 84) * mm, "end": v(94, 84) * mm});
            skLineSegment(sketch, "E2.8.2.0", {"start": v(94, 74) * mm, "end": v(94, 66) * mm});
            skLineSegment(sketch, "E2.8.2.1", {"start": v(86, 74) * mm, "end": v(86, 66) * mm});
            skLineSegment(sketch, "E2.8.2.2", {"start": v(86, 66) * mm, "end": v(94, 66) * mm});
            skLineSegment(sketch, "E2.8.2.3", {"start": v(86, 74) * mm, "end": v(94, 74) * mm});
            skLineSegment(sketch, "E2.8.3.0", {"start": v(94, 64) * mm, "end": v(94, 56) * mm});
            skLineSegment(sketch, "E2.8.3.1", {"start": v(86, 64) * mm, "end": v(86, 56) * mm});
            skLineSegment(sketch, "E2.8.3.2", {"start": v(86, 56) * mm, "end": v(94, 56) * mm});
            skLineSegment(sketch, "E2.8.3.3", {"start": v(86, 64) * mm, "end": v(94, 64) * mm});
            skLineSegment(sketch, "E2.8.4.0", {"start": v(94, 54) * mm, "end": v(94, 46) * mm});
            skLineSegment(sketch, "E2.8.4.1", {"start": v(86, 54) * mm, "end": v(86, 46) * mm});
            skLineSegment(sketch, "E2.8.4.2", {"start": v(86, 46) * mm, "end": v(94, 46) * mm});
            skLineSegment(sketch, "E2.8.4.3", {"start": v(86, 54) * mm, "end": v(94, 54) * mm});
            skLineSegment(sketch, "E2.8.5.0", {"start": v(94, 44) * mm, "end": v(94, 36) * mm});
            skLineSegment(sketch, "E2.8.5.1", {"start": v(86, 44) * mm, "end": v(86, 36) * mm});
            skLineSegment(sketch, "E2.8.5.2", {"start": v(86, 36) * mm, "end": v(94, 36) * mm});
            skLineSegment(sketch, "E2.8.5.3", {"start": v(86, 44) * mm, "end": v(94, 44) * mm});
            skLineSegment(sketch, "E2.8.6.0", {"start": v(94, 34) * mm, "end": v(94, 26) * mm});
            skLineSegment(sketch, "E2.8.6.1", {"start": v(86, 34) * mm, "end": v(86, 26) * mm});
            skLineSegment(sketch, "E2.8.6.2", {"start": v(86, 26) * mm, "end": v(94, 26) * mm});
            skLineSegment(sketch, "E2.8.6.3", {"start": v(86, 34) * mm, "end": v(94, 34) * mm});
            skLineSegment(sketch, "E2.8.7.0", {"start": v(94, 24) * mm, "end": v(94, 16) * mm});
            skLineSegment(sketch, "E2.8.7.1", {"start": v(86, 24) * mm, "end": v(86, 16) * mm});
            skLineSegment(sketch, "E2.8.7.2", {"start": v(86, 16) * mm, "end": v(94, 16) * mm});
            skLineSegment(sketch, "E2.8.7.3", {"start": v(86, 24) * mm, "end": v(94, 24) * mm});
            skLineSegment(sketch, "E2.8.8.0", {"start": v(94, 14) * mm, "end": v(94, 6) * mm});
            skLineSegment(sketch, "E2.8.8.1", {"start": v(86, 14) * mm, "end": v(86, 6) * mm});
            skLineSegment(sketch, "E2.8.8.2", {"start": v(86, 6) * mm, "end": v(94, 6) * mm});
            skLineSegment(sketch, "E2.8.8.3", {"start": v(86, 14) * mm, "end": v(94, 14) * mm});
            skLineSegment(sketch, "E2.9.0.0", {"start": v(104, 94) * mm, "end": v(104, 86) * mm});
            skLineSegment(sketch, "E2.9.0.1", {"start": v(96, 94) * mm, "end": v(96, 86) * mm});
            skLineSegment(sketch, "E2.9.0.2", {"start": v(96, 86) * mm, "end": v(104, 86) * mm});
            skLineSegment(sketch, "E2.9.0.3", {"start": v(96, 94) * mm, "end": v(104, 94) * mm});
            skLineSegment(sketch, "E2.9.1.0", {"start": v(104, 84) * mm, "end": v(104, 76) * mm});
            skLineSegment(sketch, "E2.9.1.1", {"start": v(96, 84) * mm, "end": v(96, 76) * mm});
            skLineSegment(sketch, "E2.9.1.2", {"start": v(96, 76) * mm, "end": v(104, 76) * mm});
            skLineSegment(sketch, "E2.9.1.3", {"start": v(96, 84) * mm, "end": v(104, 84) * mm});
            skLineSegment(sketch, "E2.9.2.0", {"start": v(104, 74) * mm, "end": v(104, 66) * mm});
            skLineSegment(sketch, "E2.9.2.1", {"start": v(96, 74) * mm, "end": v(96, 66) * mm});
            skLineSegment(sketch, "E2.9.2.2", {"start": v(96, 66) * mm, "end": v(104, 66) * mm});
            skLineSegment(sketch, "E2.9.2.3", {"start": v(96, 74) * mm, "end": v(104, 74) * mm});
            skLineSegment(sketch, "E2.9.3.0", {"start": v(104, 64) * mm, "end": v(104, 56) * mm});
            skLineSegment(sketch, "E2.9.3.1", {"start": v(96, 64) * mm, "end": v(96, 56) * mm});
            skLineSegment(sketch, "E2.9.3.2", {"start": v(96, 56) * mm, "end": v(104, 56) * mm});
            skLineSegment(sketch, "E2.9.3.3", {"start": v(96, 64) * mm, "end": v(104, 64) * mm});
            skLineSegment(sketch, "E2.9.4.0", {"start": v(104, 54) * mm, "end": v(104, 46) * mm});
            skLineSegment(sketch, "E2.9.4.1", {"start": v(96, 54) * mm, "end": v(96, 46) * mm});
            skLineSegment(sketch, "E2.9.4.2", {"start": v(96, 46) * mm, "end": v(104, 46) * mm});
            skLineSegment(sketch, "E2.9.4.3", {"start": v(96, 54) * mm, "end": v(104, 54) * mm});
            skLineSegment(sketch, "E2.9.5.0", {"start": v(104, 44) * mm, "end": v(104, 36) * mm});
            skLineSegment(sketch, "E2.9.5.1", {"start": v(96, 44) * mm, "end": v(96, 36) * mm});
            skLineSegment(sketch, "E2.9.5.2", {"start": v(96, 36) * mm, "end": v(104, 36) * mm});
            skLineSegment(sketch, "E2.9.5.3", {"start": v(96, 44) * mm, "end": v(104, 44) * mm});
            skLineSegment(sketch, "E2.9.6.0", {"start": v(104, 34) * mm, "end": v(104, 26) * mm});
            skLineSegment(sketch, "E2.9.6.1", {"start": v(96, 34) * mm, "end": v(96, 26) * mm});
            skLineSegment(sketch, "E2.9.6.2", {"start": v(96, 26) * mm, "end": v(104, 26) * mm});
            skLineSegment(sketch, "E2.9.6.3", {"start": v(96, 34) * mm, "end": v(104, 34) * mm});
            skLineSegment(sketch, "E2.9.7.0", {"start": v(104, 24) * mm, "end": v(104, 16) * mm});
            skLineSegment(sketch, "E2.9.7.1", {"start": v(96, 24) * mm, "end": v(96, 16) * mm});
            skLineSegment(sketch, "E2.9.7.2", {"start": v(96, 16) * mm, "end": v(104, 16) * mm});
            skLineSegment(sketch, "E2.9.7.3", {"start": v(96, 24) * mm, "end": v(104, 24) * mm});
            skLineSegment(sketch, "E2.9.8.0", {"start": v(104, 14) * mm, "end": v(104, 6) * mm});
            skLineSegment(sketch, "E2.9.8.1", {"start": v(96, 14) * mm, "end": v(96, 6) * mm});
            skLineSegment(sketch, "E2.9.8.2", {"start": v(96, 6) * mm, "end": v(104, 6) * mm});
            skLineSegment(sketch, "E2.9.8.3", {"start": v(96, 14) * mm, "end": v(104, 14) * mm});
            skLineSegment(sketch, "E2.10.0.0", {"start": v(114, 94) * mm, "end": v(114, 86) * mm});
            skLineSegment(sketch, "E2.10.0.1", {"start": v(106, 94) * mm, "end": v(106, 86) * mm});
            skLineSegment(sketch, "E2.10.0.2", {"start": v(106, 86) * mm, "end": v(114, 86) * mm});
            skLineSegment(sketch, "E2.10.0.3", {"start": v(106, 94) * mm, "end": v(114, 94) * mm});
            skLineSegment(sketch, "E2.10.1.0", {"start": v(114, 84) * mm, "end": v(114, 76) * mm});
            skLineSegment(sketch, "E2.10.1.1", {"start": v(106, 84) * mm, "end": v(106, 76) * mm});
            skLineSegment(sketch, "E2.10.1.2", {"start": v(106, 76) * mm, "end": v(114, 76) * mm});
            skLineSegment(sketch, "E2.10.1.3", {"start": v(106, 84) * mm, "end": v(114, 84) * mm});
            skLineSegment(sketch, "E2.10.2.0", {"start": v(114, 74) * mm, "end": v(114, 66) * mm});
            skLineSegment(sketch, "E2.10.2.1", {"start": v(106, 74) * mm, "end": v(106, 66) * mm});
            skLineSegment(sketch, "E2.10.2.2", {"start": v(106, 66) * mm, "end": v(114, 66) * mm});
            skLineSegment(sketch, "E2.10.2.3", {"start": v(106, 74) * mm, "end": v(114, 74) * mm});
            skLineSegment(sketch, "E2.10.3.0", {"start": v(114, 64) * mm, "end": v(114, 56) * mm});
            skLineSegment(sketch, "E2.10.3.1", {"start": v(106, 64) * mm, "end": v(106, 56) * mm});
            skLineSegment(sketch, "E2.10.3.2", {"start": v(106, 56) * mm, "end": v(114, 56) * mm});
            skLineSegment(sketch, "E2.10.3.3", {"start": v(106, 64) * mm, "end": v(114, 64) * mm});
            skLineSegment(sketch, "E2.10.4.0", {"start": v(114, 54) * mm, "end": v(114, 46) * mm});
            skLineSegment(sketch, "E2.10.4.1", {"start": v(106, 54) * mm, "end": v(106, 46) * mm});
            skLineSegment(sketch, "E2.10.4.2", {"start": v(106, 46) * mm, "end": v(114, 46) * mm});
            skLineSegment(sketch, "E2.10.4.3", {"start": v(106, 54) * mm, "end": v(114, 54) * mm});
            skLineSegment(sketch, "E2.10.5.0", {"start": v(114, 44) * mm, "end": v(114, 36) * mm});
            skLineSegment(sketch, "E2.10.5.1", {"start": v(106, 44) * mm, "end": v(106, 36) * mm});
            skLineSegment(sketch, "E2.10.5.2", {"start": v(106, 36) * mm, "end": v(114, 36) * mm});
            skLineSegment(sketch, "E2.10.5.3", {"start": v(106, 44) * mm, "end": v(114, 44) * mm});
            skLineSegment(sketch, "E2.10.6.0", {"start": v(114, 34) * mm, "end": v(114, 26) * mm});
            skLineSegment(sketch, "E2.10.6.1", {"start": v(106, 34) * mm, "end": v(106, 26) * mm});
            skLineSegment(sketch, "E2.10.6.2", {"start": v(106, 26) * mm, "end": v(114, 26) * mm});
            skLineSegment(sketch, "E2.10.6.3", {"start": v(106, 34) * mm, "end": v(114, 34) * mm});
            skLineSegment(sketch, "E2.10.7.0", {"start": v(114, 24) * mm, "end": v(114, 16) * mm});
            skLineSegment(sketch, "E2.10.7.1", {"start": v(106, 24) * mm, "end": v(106, 16) * mm});
            skLineSegment(sketch, "E2.10.7.2", {"start": v(106, 16) * mm, "end": v(114, 16) * mm});
            skLineSegment(sketch, "E2.10.7.3", {"start": v(106, 24) * mm, "end": v(114, 24) * mm});
            skLineSegment(sketch, "E2.10.8.0", {"start": v(114, 14) * mm, "end": v(114, 6) * mm});
            skLineSegment(sketch, "E2.10.8.1", {"start": v(106, 14) * mm, "end": v(106, 6) * mm});
            skLineSegment(sketch, "E2.10.8.2", {"start": v(106, 6) * mm, "end": v(114, 6) * mm});
            skLineSegment(sketch, "E2.10.8.3", {"start": v(106, 14) * mm, "end": v(114, 14) * mm});
            skLineSegment(sketch, "E2.11.0.0", {"start": v(124, 94) * mm, "end": v(124, 86) * mm});
            skLineSegment(sketch, "E2.11.0.1", {"start": v(116, 94) * mm, "end": v(116, 86) * mm});
            skLineSegment(sketch, "E2.11.0.2", {"start": v(116, 86) * mm, "end": v(124, 86) * mm});
            skLineSegment(sketch, "E2.11.0.3", {"start": v(116, 94) * mm, "end": v(124, 94) * mm});
            skLineSegment(sketch, "E2.11.1.0", {"start": v(124, 84) * mm, "end": v(124, 76) * mm});
            skLineSegment(sketch, "E2.11.1.1", {"start": v(116, 84) * mm, "end": v(116, 76) * mm});
            skLineSegment(sketch, "E2.11.1.2", {"start": v(116, 76) * mm, "end": v(124, 76) * mm});
            skLineSegment(sketch, "E2.11.1.3", {"start": v(116, 84) * mm, "end": v(124, 84) * mm});
            skLineSegment(sketch, "E2.11.2.0", {"start": v(124, 74) * mm, "end": v(124, 66) * mm});
            skLineSegment(sketch, "E2.11.2.1", {"start": v(116, 74) * mm, "end": v(116, 66) * mm});
            skLineSegment(sketch, "E2.11.2.2", {"start": v(116, 66) * mm, "end": v(124, 66) * mm});
            skLineSegment(sketch, "E2.11.2.3", {"start": v(116, 74) * mm, "end": v(124, 74) * mm});
            skLineSegment(sketch, "E2.11.3.0", {"start": v(124, 64) * mm, "end": v(124, 56) * mm});
            skLineSegment(sketch, "E2.11.3.1", {"start": v(116, 64) * mm, "end": v(116, 56) * mm});
            skLineSegment(sketch, "E2.11.3.2", {"start": v(116, 56) * mm, "end": v(124, 56) * mm});
            skLineSegment(sketch, "E2.11.3.3", {"start": v(116, 64) * mm, "end": v(124, 64) * mm});
            skLineSegment(sketch, "E2.11.4.0", {"start": v(124, 54) * mm, "end": v(124, 46) * mm});
            skLineSegment(sketch, "E2.11.4.1", {"start": v(116, 54) * mm, "end": v(116, 46) * mm});
            skLineSegment(sketch, "E2.11.4.2", {"start": v(116, 46) * mm, "end": v(124, 46) * mm});
            skLineSegment(sketch, "E2.11.4.3", {"start": v(116, 54) * mm, "end": v(124, 54) * mm});
            skLineSegment(sketch, "E2.11.5.0", {"start": v(124, 44) * mm, "end": v(124, 36) * mm});
            skLineSegment(sketch, "E2.11.5.1", {"start": v(116, 44) * mm, "end": v(116, 36) * mm});
            skLineSegment(sketch, "E2.11.5.2", {"start": v(116, 36) * mm, "end": v(124, 36) * mm});
            skLineSegment(sketch, "E2.11.5.3", {"start": v(116, 44) * mm, "end": v(124, 44) * mm});
            skLineSegment(sketch, "E2.11.6.0", {"start": v(124, 34) * mm, "end": v(124, 26) * mm});
            skLineSegment(sketch, "E2.11.6.1", {"start": v(116, 34) * mm, "end": v(116, 26) * mm});
            skLineSegment(sketch, "E2.11.6.2", {"start": v(116, 26) * mm, "end": v(124, 26) * mm});
            skLineSegment(sketch, "E2.11.6.3", {"start": v(116, 34) * mm, "end": v(124, 34) * mm});
            skLineSegment(sketch, "E2.11.7.0", {"start": v(124, 24) * mm, "end": v(124, 16) * mm});
            skLineSegment(sketch, "E2.11.7.1", {"start": v(116, 24) * mm, "end": v(116, 16) * mm});
            skLineSegment(sketch, "E2.11.7.2", {"start": v(116, 16) * mm, "end": v(124, 16) * mm});
            skLineSegment(sketch, "E2.11.7.3", {"start": v(116, 24) * mm, "end": v(124, 24) * mm});
            skLineSegment(sketch, "E2.11.8.0", {"start": v(124, 14) * mm, "end": v(124, 6) * mm});
            skLineSegment(sketch, "E2.11.8.1", {"start": v(116, 14) * mm, "end": v(116, 6) * mm});
            skLineSegment(sketch, "E2.11.8.2", {"start": v(116, 6) * mm, "end": v(124, 6) * mm});
            skLineSegment(sketch, "E2.11.8.3", {"start": v(116, 14) * mm, "end": v(124, 14) * mm});
            skLineSegment(sketch, "E2.12.0.0", {"start": v(134, 94) * mm, "end": v(134, 86) * mm});
            skLineSegment(sketch, "E2.12.0.1", {"start": v(126, 94) * mm, "end": v(126, 86) * mm});
            skLineSegment(sketch, "E2.12.0.2", {"start": v(126, 86) * mm, "end": v(134, 86) * mm});
            skLineSegment(sketch, "E2.12.0.3", {"start": v(126, 94) * mm, "end": v(134, 94) * mm});
            skLineSegment(sketch, "E2.12.1.0", {"start": v(134, 84) * mm, "end": v(134, 76) * mm});
            skLineSegment(sketch, "E2.12.1.1", {"start": v(126, 84) * mm, "end": v(126, 76) * mm});
            skLineSegment(sketch, "E2.12.1.2", {"start": v(126, 76) * mm, "end": v(134, 76) * mm});
            skLineSegment(sketch, "E2.12.1.3", {"start": v(126, 84) * mm, "end": v(134, 84) * mm});
            skLineSegment(sketch, "E2.12.2.0", {"start": v(134, 74) * mm, "end": v(134, 66) * mm});
            skLineSegment(sketch, "E2.12.2.1", {"start": v(126, 74) * mm, "end": v(126, 66) * mm});
            skLineSegment(sketch, "E2.12.2.2", {"start": v(126, 66) * mm, "end": v(134, 66) * mm});
            skLineSegment(sketch, "E2.12.2.3", {"start": v(126, 74) * mm, "end": v(134, 74) * mm});
            skLineSegment(sketch, "E2.12.3.0", {"start": v(134, 64) * mm, "end": v(134, 56) * mm});
            skLineSegment(sketch, "E2.12.3.1", {"start": v(126, 64) * mm, "end": v(126, 56) * mm});
            skLineSegment(sketch, "E2.12.3.2", {"start": v(126, 56) * mm, "end": v(134, 56) * mm});
            skLineSegment(sketch, "E2.12.3.3", {"start": v(126, 64) * mm, "end": v(134, 64) * mm});
            skLineSegment(sketch, "E2.12.4.0", {"start": v(134, 54) * mm, "end": v(134, 46) * mm});
            skLineSegment(sketch, "E2.12.4.1", {"start": v(126, 54) * mm, "end": v(126, 46) * mm});
            skLineSegment(sketch, "E2.12.4.2", {"start": v(126, 46) * mm, "end": v(134, 46) * mm});
            skLineSegment(sketch, "E2.12.4.3", {"start": v(126, 54) * mm, "end": v(134, 54) * mm});
            skLineSegment(sketch, "E2.12.5.0", {"start": v(134, 44) * mm, "end": v(134, 36) * mm});
            skLineSegment(sketch, "E2.12.5.1", {"start": v(126, 44) * mm, "end": v(126, 36) * mm});
            skLineSegment(sketch, "E2.12.5.2", {"start": v(126, 36) * mm, "end": v(134, 36) * mm});
            skLineSegment(sketch, "E2.12.5.3", {"start": v(126, 44) * mm, "end": v(134, 44) * mm});
            skLineSegment(sketch, "E2.12.6.0", {"start": v(134, 34) * mm, "end": v(134, 26) * mm});
            skLineSegment(sketch, "E2.12.6.1", {"start": v(126, 34) * mm, "end": v(126, 26) * mm});
            skLineSegment(sketch, "E2.12.6.2", {"start": v(126, 26) * mm, "end": v(134, 26) * mm});
            skLineSegment(sketch, "E2.12.6.3", {"start": v(126, 34) * mm, "end": v(134, 34) * mm});
            skLineSegment(sketch, "E2.12.7.0", {"start": v(134, 24) * mm, "end": v(134, 16) * mm});
            skLineSegment(sketch, "E2.12.7.1", {"start": v(126, 24) * mm, "end": v(126, 16) * mm});
            skLineSegment(sketch, "E2.12.7.2", {"start": v(126, 16) * mm, "end": v(134, 16) * mm});
            skLineSegment(sketch, "E2.12.7.3", {"start": v(126, 24) * mm, "end": v(134, 24) * mm});
            skLineSegment(sketch, "E2.12.8.0", {"start": v(134, 14) * mm, "end": v(134, 6) * mm});
            skLineSegment(sketch, "E2.12.8.1", {"start": v(126, 14) * mm, "end": v(126, 6) * mm});
            skLineSegment(sketch, "E2.12.8.2", {"start": v(126, 6) * mm, "end": v(134, 6) * mm});
            skLineSegment(sketch, "E2.12.8.3", {"start": v(126, 14) * mm, "end": v(134, 14) * mm});
            skLineSegment(sketch, "E2.13.0.0", {"start": v(144, 94) * mm, "end": v(144, 86) * mm});
            skLineSegment(sketch, "E2.13.0.1", {"start": v(136, 94) * mm, "end": v(136, 86) * mm});
            skLineSegment(sketch, "E2.13.0.2", {"start": v(136, 86) * mm, "end": v(144, 86) * mm});
            skLineSegment(sketch, "E2.13.0.3", {"start": v(136, 94) * mm, "end": v(144, 94) * mm});
            skLineSegment(sketch, "E2.13.1.0", {"start": v(144, 84) * mm, "end": v(144, 76) * mm});
            skLineSegment(sketch, "E2.13.1.1", {"start": v(136, 84) * mm, "end": v(136, 76) * mm});
            skLineSegment(sketch, "E2.13.1.2", {"start": v(136, 76) * mm, "end": v(144, 76) * mm});
            skLineSegment(sketch, "E2.13.1.3", {"start": v(136, 84) * mm, "end": v(144, 84) * mm});
            skLineSegment(sketch, "E2.13.2.0", {"start": v(144, 74) * mm, "end": v(144, 66) * mm});
            skLineSegment(sketch, "E2.13.2.1", {"start": v(136, 74) * mm, "end": v(136, 66) * mm});
            skLineSegment(sketch, "E2.13.2.2", {"start": v(136, 66) * mm, "end": v(144, 66) * mm});
            skLineSegment(sketch, "E2.13.2.3", {"start": v(136, 74) * mm, "end": v(144, 74) * mm});
            skLineSegment(sketch, "E2.13.3.0", {"start": v(144, 64) * mm, "end": v(144, 56) * mm});
            skLineSegment(sketch, "E2.13.3.1", {"start": v(136, 64) * mm, "end": v(136, 56) * mm});
            skLineSegment(sketch, "E2.13.3.2", {"start": v(136, 56) * mm, "end": v(144, 56) * mm});
            skLineSegment(sketch, "E2.13.3.3", {"start": v(136, 64) * mm, "end": v(144, 64) * mm});
            skLineSegment(sketch, "E2.13.4.0", {"start": v(144, 54) * mm, "end": v(144, 46) * mm});
            skLineSegment(sketch, "E2.13.4.1", {"start": v(136, 54) * mm, "end": v(136, 46) * mm});
            skLineSegment(sketch, "E2.13.4.2", {"start": v(136, 46) * mm, "end": v(144, 46) * mm});
            skLineSegment(sketch, "E2.13.4.3", {"start": v(136, 54) * mm, "end": v(144, 54) * mm});
            skLineSegment(sketch, "E2.13.5.0", {"start": v(144, 44) * mm, "end": v(144, 36) * mm});
            skLineSegment(sketch, "E2.13.5.1", {"start": v(136, 44) * mm, "end": v(136, 36) * mm});
            skLineSegment(sketch, "E2.13.5.2", {"start": v(136, 36) * mm, "end": v(144, 36) * mm});
            skLineSegment(sketch, "E2.13.5.3", {"start": v(136, 44) * mm, "end": v(144, 44) * mm});
            skLineSegment(sketch, "E2.13.6.0", {"start": v(144, 34) * mm, "end": v(144, 26) * mm});
            skLineSegment(sketch, "E2.13.6.1", {"start": v(136, 34) * mm, "end": v(136, 26) * mm});
            skLineSegment(sketch, "E2.13.6.2", {"start": v(136, 26) * mm, "end": v(144, 26) * mm});
            skLineSegment(sketch, "E2.13.6.3", {"start": v(136, 34) * mm, "end": v(144, 34) * mm});
            skLineSegment(sketch, "E2.13.7.0", {"start": v(144, 24) * mm, "end": v(144, 16) * mm});
            skLineSegment(sketch, "E2.13.7.1", {"start": v(136, 24) * mm, "end": v(136, 16) * mm});
            skLineSegment(sketch, "E2.13.7.2", {"start": v(136, 16) * mm, "end": v(144, 16) * mm});
            skLineSegment(sketch, "E2.13.7.3", {"start": v(136, 24) * mm, "end": v(144, 24) * mm});
            skLineSegment(sketch, "E2.13.8.0", {"start": v(144, 14) * mm, "end": v(144, 6) * mm});
            skLineSegment(sketch, "E2.13.8.1", {"start": v(136, 14) * mm, "end": v(136, 6) * mm});
            skLineSegment(sketch, "E2.13.8.2", {"start": v(136, 6) * mm, "end": v(144, 6) * mm});
            skLineSegment(sketch, "E2.13.8.3", {"start": v(136, 14) * mm, "end": v(144, 14) * mm});
            skLineSegment(sketch, "E2.14.0.0", {"start": v(154, 94) * mm, "end": v(154, 86) * mm});
            skLineSegment(sketch, "E2.14.0.1", {"start": v(146, 94) * mm, "end": v(146, 86) * mm});
            skLineSegment(sketch, "E2.14.0.2", {"start": v(146, 86) * mm, "end": v(154, 86) * mm});
            skLineSegment(sketch, "E2.14.0.3", {"start": v(146, 94) * mm, "end": v(154, 94) * mm});
            skLineSegment(sketch, "E2.14.1.0", {"start": v(154, 84) * mm, "end": v(154, 76) * mm});
            skLineSegment(sketch, "E2.14.1.1", {"start": v(146, 84) * mm, "end": v(146, 76) * mm});
            skLineSegment(sketch, "E2.14.1.2", {"start": v(146, 76) * mm, "end": v(154, 76) * mm});
            skLineSegment(sketch, "E2.14.1.3", {"start": v(146, 84) * mm, "end": v(154, 84) * mm});
            skLineSegment(sketch, "E2.14.2.0", {"start": v(154, 74) * mm, "end": v(154, 66) * mm});
            skLineSegment(sketch, "E2.14.2.1", {"start": v(146, 74) * mm, "end": v(146, 66) * mm});
            skLineSegment(sketch, "E2.14.2.2", {"start": v(146, 66) * mm, "end": v(154, 66) * mm});
            skLineSegment(sketch, "E2.14.2.3", {"start": v(146, 74) * mm, "end": v(154, 74) * mm});
            skLineSegment(sketch, "E2.14.3.0", {"start": v(154, 64) * mm, "end": v(154, 56) * mm});
            skLineSegment(sketch, "E2.14.3.1", {"start": v(146, 64) * mm, "end": v(146, 56) * mm});
            skLineSegment(sketch, "E2.14.3.2", {"start": v(146, 56) * mm, "end": v(154, 56) * mm});
            skLineSegment(sketch, "E2.14.3.3", {"start": v(146, 64) * mm, "end": v(154, 64) * mm});
            skLineSegment(sketch, "E2.14.4.0", {"start": v(154, 54) * mm, "end": v(154, 46) * mm});
            skLineSegment(sketch, "E2.14.4.1", {"start": v(146, 54) * mm, "end": v(146, 46) * mm});
            skLineSegment(sketch, "E2.14.4.2", {"start": v(146, 46) * mm, "end": v(154, 46) * mm});
            skLineSegment(sketch, "E2.14.4.3", {"start": v(146, 54) * mm, "end": v(154, 54) * mm});
            skLineSegment(sketch, "E2.14.5.0", {"start": v(154, 44) * mm, "end": v(154, 36) * mm});
            skLineSegment(sketch, "E2.14.5.1", {"start": v(146, 44) * mm, "end": v(146, 36) * mm});
            skLineSegment(sketch, "E2.14.5.2", {"start": v(146, 36) * mm, "end": v(154, 36) * mm});
            skLineSegment(sketch, "E2.14.5.3", {"start": v(146, 44) * mm, "end": v(154, 44) * mm});
            skLineSegment(sketch, "E2.14.6.0", {"start": v(154, 34) * mm, "end": v(154, 26) * mm});
            skLineSegment(sketch, "E2.14.6.1", {"start": v(146, 34) * mm, "end": v(146, 26) * mm});
            skLineSegment(sketch, "E2.14.6.2", {"start": v(146, 26) * mm, "end": v(154, 26) * mm});
            skLineSegment(sketch, "E2.14.6.3", {"start": v(146, 34) * mm, "end": v(154, 34) * mm});
            skLineSegment(sketch, "E2.14.7.0", {"start": v(154, 24) * mm, "end": v(154, 16) * mm});
            skLineSegment(sketch, "E2.14.7.1", {"start": v(146, 24) * mm, "end": v(146, 16) * mm});
            skLineSegment(sketch, "E2.14.7.2", {"start": v(146, 16) * mm, "end": v(154, 16) * mm});
            skLineSegment(sketch, "E2.14.7.3", {"start": v(146, 24) * mm, "end": v(154, 24) * mm});
            skLineSegment(sketch, "E2.14.8.0", {"start": v(154, 14) * mm, "end": v(154, 6) * mm});
            skLineSegment(sketch, "E2.14.8.1", {"start": v(146, 14) * mm, "end": v(146, 6) * mm});
            skLineSegment(sketch, "E2.14.8.2", {"start": v(146, 6) * mm, "end": v(154, 6) * mm});
            skLineSegment(sketch, "E2.14.8.3", {"start": v(146, 14) * mm, "end": v(154, 14) * mm});
            skLineSegment(sketch, "E2.15.0.0", {"start": v(164, 94) * mm, "end": v(164, 86) * mm});
            skLineSegment(sketch, "E2.15.0.1", {"start": v(156, 94) * mm, "end": v(156, 86) * mm});
            skLineSegment(sketch, "E2.15.0.2", {"start": v(156, 86) * mm, "end": v(164, 86) * mm});
            skLineSegment(sketch, "E2.15.0.3", {"start": v(156, 94) * mm, "end": v(164, 94) * mm});
            skLineSegment(sketch, "E2.15.1.0", {"start": v(164, 84) * mm, "end": v(164, 76) * mm});
            skLineSegment(sketch, "E2.15.1.1", {"start": v(156, 84) * mm, "end": v(156, 76) * mm});
            skLineSegment(sketch, "E2.15.1.2", {"start": v(156, 76) * mm, "end": v(164, 76) * mm});
            skLineSegment(sketch, "E2.15.1.3", {"start": v(156, 84) * mm, "end": v(164, 84) * mm});
            skLineSegment(sketch, "E2.15.2.0", {"start": v(164, 74) * mm, "end": v(164, 66) * mm});
            skLineSegment(sketch, "E2.15.2.1", {"start": v(156, 74) * mm, "end": v(156, 66) * mm});
            skLineSegment(sketch, "E2.15.2.2", {"start": v(156, 66) * mm, "end": v(164, 66) * mm});
            skLineSegment(sketch, "E2.15.2.3", {"start": v(156, 74) * mm, "end": v(164, 74) * mm});
            skLineSegment(sketch, "E2.15.3.0", {"start": v(164, 64) * mm, "end": v(164, 56) * mm});
            skLineSegment(sketch, "E2.15.3.1", {"start": v(156, 64) * mm, "end": v(156, 56) * mm});
            skLineSegment(sketch, "E2.15.3.2", {"start": v(156, 56) * mm, "end": v(164, 56) * mm});
            skLineSegment(sketch, "E2.15.3.3", {"start": v(156, 64) * mm, "end": v(164, 64) * mm});
            skLineSegment(sketch, "E2.15.4.0", {"start": v(164, 54) * mm, "end": v(164, 46) * mm});
            skLineSegment(sketch, "E2.15.4.1", {"start": v(156, 54) * mm, "end": v(156, 46) * mm});
            skLineSegment(sketch, "E2.15.4.2", {"start": v(156, 46) * mm, "end": v(164, 46) * mm});
            skLineSegment(sketch, "E2.15.4.3", {"start": v(156, 54) * mm, "end": v(164, 54) * mm});
            skLineSegment(sketch, "E2.15.5.0", {"start": v(164, 44) * mm, "end": v(164, 36) * mm});
            skLineSegment(sketch, "E2.15.5.1", {"start": v(156, 44) * mm, "end": v(156, 36) * mm});
            skLineSegment(sketch, "E2.15.5.2", {"start": v(156, 36) * mm, "end": v(164, 36) * mm});
            skLineSegment(sketch, "E2.15.5.3", {"start": v(156, 44) * mm, "end": v(164, 44) * mm});
            skLineSegment(sketch, "E2.15.6.0", {"start": v(164, 34) * mm, "end": v(164, 26) * mm});
            skLineSegment(sketch, "E2.15.6.1", {"start": v(156, 34) * mm, "end": v(156, 26) * mm});
            skLineSegment(sketch, "E2.15.6.2", {"start": v(156, 26) * mm, "end": v(164, 26) * mm});
            skLineSegment(sketch, "E2.15.6.3", {"start": v(156, 34) * mm, "end": v(164, 34) * mm});
            skLineSegment(sketch, "E2.15.7.0", {"start": v(164, 24) * mm, "end": v(164, 16) * mm});
            skLineSegment(sketch, "E2.15.7.1", {"start": v(156, 24) * mm, "end": v(156, 16) * mm});
            skLineSegment(sketch, "E2.15.7.2", {"start": v(156, 16) * mm, "end": v(164, 16) * mm});
            skLineSegment(sketch, "E2.15.7.3", {"start": v(156, 24) * mm, "end": v(164, 24) * mm});
            skLineSegment(sketch, "E2.15.8.0", {"start": v(164, 14) * mm, "end": v(164, 6) * mm});
            skLineSegment(sketch, "E2.15.8.1", {"start": v(156, 14) * mm, "end": v(156, 6) * mm});
            skLineSegment(sketch, "E2.15.8.2", {"start": v(156, 6) * mm, "end": v(164, 6) * mm});
            skLineSegment(sketch, "E2.15.8.3", {"start": v(156, 14) * mm, "end": v(164, 14) * mm});
            skLineSegment(sketch, "E2.16.0.0", {"start": v(174, 94) * mm, "end": v(174, 86) * mm});
            skLineSegment(sketch, "E2.16.0.1", {"start": v(166, 94) * mm, "end": v(166, 86) * mm});
            skLineSegment(sketch, "E2.16.0.2", {"start": v(166, 86) * mm, "end": v(174, 86) * mm});
            skLineSegment(sketch, "E2.16.0.3", {"start": v(166, 94) * mm, "end": v(174, 94) * mm});
            skLineSegment(sketch, "E2.16.1.0", {"start": v(174, 84) * mm, "end": v(174, 76) * mm});
            skLineSegment(sketch, "E2.16.1.1", {"start": v(166, 84) * mm, "end": v(166, 76) * mm});
            skLineSegment(sketch, "E2.16.1.2", {"start": v(166, 76) * mm, "end": v(174, 76) * mm});
            skLineSegment(sketch, "E2.16.1.3", {"start": v(166, 84) * mm, "end": v(174, 84) * mm});
            skLineSegment(sketch, "E2.16.2.0", {"start": v(174, 74) * mm, "end": v(174, 66) * mm});
            skLineSegment(sketch, "E2.16.2.1", {"start": v(166, 74) * mm, "end": v(166, 66) * mm});
            skLineSegment(sketch, "E2.16.2.2", {"start": v(166, 66) * mm, "end": v(174, 66) * mm});
            skLineSegment(sketch, "E2.16.2.3", {"start": v(166, 74) * mm, "end": v(174, 74) * mm});
            skLineSegment(sketch, "E2.16.3.0", {"start": v(174, 64) * mm, "end": v(174, 56) * mm});
            skLineSegment(sketch, "E2.16.3.1", {"start": v(166, 64) * mm, "end": v(166, 56) * mm});
            skLineSegment(sketch, "E2.16.3.2", {"start": v(166, 56) * mm, "end": v(174, 56) * mm});
            skLineSegment(sketch, "E2.16.3.3", {"start": v(166, 64) * mm, "end": v(174, 64) * mm});
            skLineSegment(sketch, "E2.16.4.0", {"start": v(174, 54) * mm, "end": v(174, 46) * mm});
            skLineSegment(sketch, "E2.16.4.1", {"start": v(166, 54) * mm, "end": v(166, 46) * mm});
            skLineSegment(sketch, "E2.16.4.2", {"start": v(166, 46) * mm, "end": v(174, 46) * mm});
            skLineSegment(sketch, "E2.16.4.3", {"start": v(166, 54) * mm, "end": v(174, 54) * mm});
            skLineSegment(sketch, "E2.16.5.0", {"start": v(174, 44) * mm, "end": v(174, 36) * mm});
            skLineSegment(sketch, "E2.16.5.1", {"start": v(166, 44) * mm, "end": v(166, 36) * mm});
            skLineSegment(sketch, "E2.16.5.2", {"start": v(166, 36) * mm, "end": v(174, 36) * mm});
            skLineSegment(sketch, "E2.16.5.3", {"start": v(166, 44) * mm, "end": v(174, 44) * mm});
            skLineSegment(sketch, "E2.16.6.0", {"start": v(174, 34) * mm, "end": v(174, 26) * mm});
            skLineSegment(sketch, "E2.16.6.1", {"start": v(166, 34) * mm, "end": v(166, 26) * mm});
            skLineSegment(sketch, "E2.16.6.2", {"start": v(166, 26) * mm, "end": v(174, 26) * mm});
            skLineSegment(sketch, "E2.16.6.3", {"start": v(166, 34) * mm, "end": v(174, 34) * mm});
            skLineSegment(sketch, "E2.16.7.0", {"start": v(174, 24) * mm, "end": v(174, 16) * mm});
            skLineSegment(sketch, "E2.16.7.1", {"start": v(166, 24) * mm, "end": v(166, 16) * mm});
            skLineSegment(sketch, "E2.16.7.2", {"start": v(166, 16) * mm, "end": v(174, 16) * mm});
            skLineSegment(sketch, "E2.16.7.3", {"start": v(166, 24) * mm, "end": v(174, 24) * mm});
            skLineSegment(sketch, "E2.16.8.0", {"start": v(174, 14) * mm, "end": v(174, 6) * mm});
            skLineSegment(sketch, "E2.16.8.1", {"start": v(166, 14) * mm, "end": v(166, 6) * mm});
            skLineSegment(sketch, "E2.16.8.2", {"start": v(166, 6) * mm, "end": v(174, 6) * mm});
            skLineSegment(sketch, "E2.16.8.3", {"start": v(166, 14) * mm, "end": v(174, 14) * mm});
            skLineSegment(sketch, "E2.17.0.0", {"start": v(184, 94) * mm, "end": v(184, 86) * mm});
            skLineSegment(sketch, "E2.17.0.1", {"start": v(176, 94) * mm, "end": v(176, 86) * mm});
            skLineSegment(sketch, "E2.17.0.2", {"start": v(176, 86) * mm, "end": v(184, 86) * mm});
            skLineSegment(sketch, "E2.17.0.3", {"start": v(176, 94) * mm, "end": v(184, 94) * mm});
            skLineSegment(sketch, "E2.17.1.0", {"start": v(184, 84) * mm, "end": v(184, 76) * mm});
            skLineSegment(sketch, "E2.17.1.1", {"start": v(176, 84) * mm, "end": v(176, 76) * mm});
            skLineSegment(sketch, "E2.17.1.2", {"start": v(176, 76) * mm, "end": v(184, 76) * mm});
            skLineSegment(sketch, "E2.17.1.3", {"start": v(176, 84) * mm, "end": v(184, 84) * mm});
            skLineSegment(sketch, "E2.17.2.0", {"start": v(184, 74) * mm, "end": v(184, 66) * mm});
            skLineSegment(sketch, "E2.17.2.1", {"start": v(176, 74) * mm, "end": v(176, 66) * mm});
            skLineSegment(sketch, "E2.17.2.2", {"start": v(176, 66) * mm, "end": v(184, 66) * mm});
            skLineSegment(sketch, "E2.17.2.3", {"start": v(176, 74) * mm, "end": v(184, 74) * mm});
            skLineSegment(sketch, "E2.17.3.0", {"start": v(184, 64) * mm, "end": v(184, 56) * mm});
            skLineSegment(sketch, "E2.17.3.1", {"start": v(176, 64) * mm, "end": v(176, 56) * mm});
            skLineSegment(sketch, "E2.17.3.2", {"start": v(176, 56) * mm, "end": v(184, 56) * mm});
            skLineSegment(sketch, "E2.17.3.3", {"start": v(176, 64) * mm, "end": v(184, 64) * mm});
            skLineSegment(sketch, "E2.17.4.0", {"start": v(184, 54) * mm, "end": v(184, 46) * mm});
            skLineSegment(sketch, "E2.17.4.1", {"start": v(176, 54) * mm, "end": v(176, 46) * mm});
            skLineSegment(sketch, "E2.17.4.2", {"start": v(176, 46) * mm, "end": v(184, 46) * mm});
            skLineSegment(sketch, "E2.17.4.3", {"start": v(176, 54) * mm, "end": v(184, 54) * mm});
            skLineSegment(sketch, "E2.17.5.0", {"start": v(184, 44) * mm, "end": v(184, 36) * mm});
            skLineSegment(sketch, "E2.17.5.1", {"start": v(176, 44) * mm, "end": v(176, 36) * mm});
            skLineSegment(sketch, "E2.17.5.2", {"start": v(176, 36) * mm, "end": v(184, 36) * mm});
            skLineSegment(sketch, "E2.17.5.3", {"start": v(176, 44) * mm, "end": v(184, 44) * mm});
            skLineSegment(sketch, "E2.17.6.0", {"start": v(184, 34) * mm, "end": v(184, 26) * mm});
            skLineSegment(sketch, "E2.17.6.1", {"start": v(176, 34) * mm, "end": v(176, 26) * mm});
            skLineSegment(sketch, "E2.17.6.2", {"start": v(176, 26) * mm, "end": v(184, 26) * mm});
            skLineSegment(sketch, "E2.17.6.3", {"start": v(176, 34) * mm, "end": v(184, 34) * mm});
            skLineSegment(sketch, "E2.17.7.0", {"start": v(184, 24) * mm, "end": v(184, 16) * mm});
            skLineSegment(sketch, "E2.17.7.1", {"start": v(176, 24) * mm, "end": v(176, 16) * mm});
            skLineSegment(sketch, "E2.17.7.2", {"start": v(176, 16) * mm, "end": v(184, 16) * mm});
            skLineSegment(sketch, "E2.17.7.3", {"start": v(176, 24) * mm, "end": v(184, 24) * mm});
            skLineSegment(sketch, "E2.17.8.0", {"start": v(184, 14) * mm, "end": v(184, 6) * mm});
            skLineSegment(sketch, "E2.17.8.1", {"start": v(176, 14) * mm, "end": v(176, 6) * mm});
            skLineSegment(sketch, "E2.17.8.2", {"start": v(176, 6) * mm, "end": v(184, 6) * mm});
            skLineSegment(sketch, "E2.17.8.3", {"start": v(176, 14) * mm, "end": v(184, 14) * mm});
            skLineSegment(sketch, "E2.18.0.0", {"start": v(194, 94) * mm, "end": v(194, 86) * mm});
            skLineSegment(sketch, "E2.18.0.1", {"start": v(186, 94) * mm, "end": v(186, 86) * mm});
            skLineSegment(sketch, "E2.18.0.2", {"start": v(186, 86) * mm, "end": v(194, 86) * mm});
            skLineSegment(sketch, "E2.18.0.3", {"start": v(186, 94) * mm, "end": v(194, 94) * mm});
            skLineSegment(sketch, "E2.18.1.0", {"start": v(194, 84) * mm, "end": v(194, 76) * mm});
            skLineSegment(sketch, "E2.18.1.1", {"start": v(186, 84) * mm, "end": v(186, 76) * mm});
            skLineSegment(sketch, "E2.18.1.2", {"start": v(186, 76) * mm, "end": v(194, 76) * mm});
            skLineSegment(sketch, "E2.18.1.3", {"start": v(186, 84) * mm, "end": v(194, 84) * mm});
            skLineSegment(sketch, "E2.18.2.0", {"start": v(194, 74) * mm, "end": v(194, 66) * mm});
            skLineSegment(sketch, "E2.18.2.1", {"start": v(186, 74) * mm, "end": v(186, 66) * mm});
            skLineSegment(sketch, "E2.18.2.2", {"start": v(186, 66) * mm, "end": v(194, 66) * mm});
            skLineSegment(sketch, "E2.18.2.3", {"start": v(186, 74) * mm, "end": v(194, 74) * mm});
            skLineSegment(sketch, "E2.18.3.0", {"start": v(194, 64) * mm, "end": v(194, 56) * mm});
            skLineSegment(sketch, "E2.18.3.1", {"start": v(186, 64) * mm, "end": v(186, 56) * mm});
            skLineSegment(sketch, "E2.18.3.2", {"start": v(186, 56) * mm, "end": v(194, 56) * mm});
            skLineSegment(sketch, "E2.18.3.3", {"start": v(186, 64) * mm, "end": v(194, 64) * mm});
            skLineSegment(sketch, "E2.18.4.0", {"start": v(194, 54) * mm, "end": v(194, 46) * mm});
            skLineSegment(sketch, "E2.18.4.1", {"start": v(186, 54) * mm, "end": v(186, 46) * mm});
            skLineSegment(sketch, "E2.18.4.2", {"start": v(186, 46) * mm, "end": v(194, 46) * mm});
            skLineSegment(sketch, "E2.18.4.3", {"start": v(186, 54) * mm, "end": v(194, 54) * mm});
            skLineSegment(sketch, "E2.18.5.0", {"start": v(194, 44) * mm, "end": v(194, 36) * mm});
            skLineSegment(sketch, "E2.18.5.1", {"start": v(186, 44) * mm, "end": v(186, 36) * mm});
            skLineSegment(sketch, "E2.18.5.2", {"start": v(186, 36) * mm, "end": v(194, 36) * mm});
            skLineSegment(sketch, "E2.18.5.3", {"start": v(186, 44) * mm, "end": v(194, 44) * mm});
            skLineSegment(sketch, "E2.18.6.0", {"start": v(194, 34) * mm, "end": v(194, 26) * mm});
            skLineSegment(sketch, "E2.18.6.1", {"start": v(186, 34) * mm, "end": v(186, 26) * mm});
            skLineSegment(sketch, "E2.18.6.2", {"start": v(186, 26) * mm, "end": v(194, 26) * mm});
            skLineSegment(sketch, "E2.18.6.3", {"start": v(186, 34) * mm, "end": v(194, 34) * mm});
            skLineSegment(sketch, "E2.18.7.0", {"start": v(194, 24) * mm, "end": v(194, 16) * mm});
            skLineSegment(sketch, "E2.18.7.1", {"start": v(186, 24) * mm, "end": v(186, 16) * mm});
            skLineSegment(sketch, "E2.18.7.2", {"start": v(186, 16) * mm, "end": v(194, 16) * mm});
            skLineSegment(sketch, "E2.18.7.3", {"start": v(186, 24) * mm, "end": v(194, 24) * mm});
            skLineSegment(sketch, "E2.18.8.0", {"start": v(194, 14) * mm, "end": v(194, 6) * mm});
            skLineSegment(sketch, "E2.18.8.1", {"start": v(186, 14) * mm, "end": v(186, 6) * mm});
            skLineSegment(sketch, "E2.18.8.2", {"start": v(186, 6) * mm, "end": v(194, 6) * mm});
            skLineSegment(sketch, "E2.18.8.3", {"start": v(186, 14) * mm, "end": v(194, 14) * mm});
            skLineSegment(sketch, "E2.direction1", {"start": v(6, 86) * mm, "end": v(16, 86) * mm, "construction": true});
            skLineSegment(sketch, "E2.direction2", {"start": v(6, 86) * mm, "end": v(6, 76) * mm, "construction": true});
            skSolve(sketch);
        }
        {
            var Q0;
            Q0=makeQuery(id+"F2.imprint","IMPRINT",FACE,{"disambiguationData":[TD([[makeQuery(id+"F2.imprint","IMPRINT",EDGE,{"derivedFrom":sQuery(id+"F2.wireOp",EDGE,"E1.bottom")}),-1.0]])]});
            var Q1;
            Q1=makeQuery(id+"F2.imprint","IMPRINT",FACE,{"disambiguationData":[TD([[makeQuery(id+"F2.imprint","IMPRINT",EDGE,{"derivedFrom":sQuery(id+"F2.wireOp",EDGE,"E2.5.2.0")}),-1.0]])]});
            var Q2;
            Q2=makeQuery(id+"F2.imprint","IMPRINT",FACE,{"disambiguationData":[TD([[makeQuery(id+"F2.imprint","IMPRINT",EDGE,{"derivedFrom":sQuery(id+"F2.wireOp",EDGE,"E2.3.4.0")}),-1.0]])]});
            var Q3;
            Q3=makeQuery(id+"F2.imprint","IMPRINT",FACE,{"disambiguationData":[TD([[makeQuery(id+"F2.imprint","IMPRINT",EDGE,{"derivedFrom":sQuery(id+"F2.wireOp",EDGE,"E2.12.3.0")}),-1.0]])]});
            var Q4;
            Q4=makeQuery(id+"F2.imprint","IMPRINT",FACE,{"disambiguationData":[TD([[makeQuery(id+"F2.imprint","IMPRINT",EDGE,{"derivedFrom":sQuery(id+"F2.wireOp",EDGE,"E2.10.5.0")}),-1.0]])]});
            var Q5;
            Q5=makeQuery(id+"F2.imprint","IMPRINT",FACE,{"disambiguationData":[TD([[makeQuery(id+"F2.imprint","IMPRINT",EDGE,{"derivedFrom":sQuery(id+"F2.wireOp",EDGE,"E2.8.7.0")}),-1.0]])]});
            var Q6;
            Q6=makeQuery(id+"F2.imprint","IMPRINT",FACE,{"disambiguationData":[TD([[makeQuery(id+"F2.imprint","IMPRINT",EDGE,{"derivedFrom":sQuery(id+"F2.wireOp",EDGE,"E2.7.0.0")}),-1.0]])]});
            var Q7;
            Q7=makeQuery(id+"F2.imprint","IMPRINT",FACE,{"disambiguationData":[TD([[makeQuery(id+"F2.imprint","IMPRINT",EDGE,{"derivedFrom":sQuery(id+"F2.wireOp",EDGE,"E2.17.6.0")}),-1.0]])]});
            var Q8;
            Q8=makeQuery(id+"F2.imprint","IMPRINT",FACE,{"disambiguationData":[TD([[makeQuery(id+"F2.imprint","IMPRINT",EDGE,{"derivedFrom":sQuery(id+"F2.wireOp",EDGE,"E2.15.8.0")}),-1.0]])]});
            var Q9;
            Q9=makeQuery(id+"F2.imprint","IMPRINT",FACE,{"disambiguationData":[TD([[makeQuery(id+"F2.imprint","IMPRINT",EDGE,{"derivedFrom":sQuery(id+"F2.wireOp",EDGE,"E2.14.1.0")}),-1.0]])]});
            var Q10;
            Q10=makeQuery(id+"F2.imprint","IMPRINT",FACE,{"disambiguationData":[TD([[makeQuery(id+"F2.imprint","IMPRINT",EDGE,{"derivedFrom":sQuery(id+"F2.wireOp",EDGE,"E2.3.2.0")}),-1.0]])]});
            var Q11;
            Q11=makeQuery(id+"F2.imprint","IMPRINT",FACE,{"disambiguationData":[TD([[makeQuery(id+"F2.imprint","IMPRINT",EDGE,{"derivedFrom":sQuery(id+"F2.wireOp",EDGE,"E2.10.3.0")}),-1.0]])]});
            var Q12;
            Q12=makeQuery(id+"F2.imprint","IMPRINT",FACE,{"disambiguationData":[TD([[makeQuery(id+"F2.imprint","IMPRINT",EDGE,{"derivedFrom":sQuery(id+"F2.wireOp",EDGE,"E2.8.5.0")}),-1.0]])]});
            var Q13;
            Q13=makeQuery(id+"F2.imprint","IMPRINT",FACE,{"disambiguationData":[TD([[makeQuery(id+"F2.imprint","IMPRINT",EDGE,{"derivedFrom":sQuery(id+"F2.wireOp",EDGE,"E2.6.7.0")}),-1.0]])]});
            var Q14;
            Q14=makeQuery(id+"F2.imprint","IMPRINT",FACE,{"disambiguationData":[TD([[makeQuery(id+"F2.imprint","IMPRINT",EDGE,{"derivedFrom":sQuery(id+"F2.wireOp",EDGE,"E2.5.0.0")}),-1.0]])]});
            var Q15;
            Q15=makeQuery(id+"F2.imprint","IMPRINT",FACE,{"disambiguationData":[TD([[makeQuery(id+"F2.imprint","IMPRINT",EDGE,{"derivedFrom":sQuery(id+"F2.wireOp",EDGE,"E2.17.4.0")}),-1.0]])]});
            var Q16;
            Q16=makeQuery(id+"F2.imprint","IMPRINT",FACE,{"disambiguationData":[TD([[makeQuery(id+"F2.imprint","IMPRINT",EDGE,{"derivedFrom":sQuery(id+"F2.wireOp",EDGE,"E2.15.6.0")}),-1.0]])]});
            var Q17;
            Q17=makeQuery(id+"F2.imprint","IMPRINT",FACE,{"disambiguationData":[TD([[makeQuery(id+"F2.imprint","IMPRINT",EDGE,{"derivedFrom":sQuery(id+"F2.wireOp",EDGE,"E2.13.8.0")}),-1.0]])]});
            var Q18;
            Q18=makeQuery(id+"F2.imprint","IMPRINT",FACE,{"disambiguationData":[TD([[makeQuery(id+"F2.imprint","IMPRINT",EDGE,{"derivedFrom":sQuery(id+"F2.wireOp",EDGE,"E2.12.1.0")}),-1.0]])]});
            var Q19;
            Q19=makeQuery(id+"F2.imprint","IMPRINT",FACE,{"disambiguationData":[TD([[makeQuery(id+"F2.imprint","IMPRINT",EDGE,{"derivedFrom":sQuery(id+"F2.wireOp",EDGE,"E2.3.3.0")}),-1.0]])]});
            var Q20;
            Q20=makeQuery(id+"F2.imprint","IMPRINT",FACE,{"disambiguationData":[TD([[makeQuery(id+"F2.imprint","IMPRINT",EDGE,{"derivedFrom":sQuery(id+"F2.wireOp",EDGE,"E2.10.4.0")}),-1.0]])]});
            var Q21;
            Q21=makeQuery(id+"F2.imprint","IMPRINT",FACE,{"disambiguationData":[TD([[makeQuery(id+"F2.imprint","IMPRINT",EDGE,{"derivedFrom":sQuery(id+"F2.wireOp",EDGE,"E2.8.6.0")}),-1.0]])]});
            var Q22;
            Q22=makeQuery(id+"F2.imprint","IMPRINT",FACE,{"disambiguationData":[TD([[makeQuery(id+"F2.imprint","IMPRINT",EDGE,{"derivedFrom":sQuery(id+"F2.wireOp",EDGE,"E2.6.8.0")}),-1.0]])]});
            var Q23;
            Q23=makeQuery(id+"F2.imprint","IMPRINT",FACE,{"disambiguationData":[TD([[makeQuery(id+"F2.imprint","IMPRINT",EDGE,{"derivedFrom":sQuery(id+"F2.wireOp",EDGE,"E2.5.1.0")}),-1.0]])]});
            var Q24;
            Q24=makeQuery(id+"F2.imprint","IMPRINT",FACE,{"disambiguationData":[TD([[makeQuery(id+"F2.imprint","IMPRINT",EDGE,{"derivedFrom":sQuery(id+"F2.wireOp",EDGE,"E2.17.5.0")}),-1.0]])]});
            var Q25;
            Q25=makeQuery(id+"F2.imprint","IMPRINT",FACE,{"disambiguationData":[TD([[makeQuery(id+"F2.imprint","IMPRINT",EDGE,{"derivedFrom":sQuery(id+"F2.wireOp",EDGE,"E2.15.7.0")}),-1.0]])]});
            var Q26;
            Q26=makeQuery(id+"F2.imprint","IMPRINT",FACE,{"disambiguationData":[TD([[makeQuery(id+"F2.imprint","IMPRINT",EDGE,{"derivedFrom":sQuery(id+"F2.wireOp",EDGE,"E2.14.0.0")}),-1.0]])]});
            var Q27;
            Q27=makeQuery(id+"F2.imprint","IMPRINT",FACE,{"disambiguationData":[TD([[makeQuery(id+"F2.imprint","IMPRINT",EDGE,{"derivedFrom":sQuery(id+"F2.wireOp",EDGE,"E2.12.2.0")}),-1.0]])]});
            var Q28;
            Q28=makeQuery(id+"F2.imprint","IMPRINT",FACE,{"disambiguationData":[TD([[makeQuery(id+"F2.imprint","IMPRINT",EDGE,{"derivedFrom":sQuery(id+"F2.wireOp",EDGE,"E2.3.5.0")}),-1.0]])]});
            var Q29;
            Q29=makeQuery(id+"F2.imprint","IMPRINT",FACE,{"disambiguationData":[TD([[makeQuery(id+"F2.imprint","IMPRINT",EDGE,{"derivedFrom":sQuery(id+"F2.wireOp",EDGE,"E2.1.7.0")}),-1.0]])]});
            var Q30;
            Q30=makeQuery(id+"F2.imprint","IMPRINT",FACE,{"disambiguationData":[TD([[makeQuery(id+"F2.imprint","IMPRINT",EDGE,{"derivedFrom":sQuery(id+"F2.wireOp",EDGE,"E2.10.6.0")}),-1.0]])]});
            var Q31;
            Q31=makeQuery(id+"F2.imprint","IMPRINT",FACE,{"disambiguationData":[TD([[makeQuery(id+"F2.imprint","IMPRINT",EDGE,{"derivedFrom":sQuery(id+"F2.wireOp",EDGE,"E2.8.8.0")}),-1.0]])]});
            var Q32;
            Q32=makeQuery(id+"F2.imprint","IMPRINT",FACE,{"disambiguationData":[TD([[makeQuery(id+"F2.imprint","IMPRINT",EDGE,{"derivedFrom":sQuery(id+"F2.wireOp",EDGE,"E2.7.1.0")}),-1.0]])]});
            var Q33;
            Q33=makeQuery(id+"F2.imprint","IMPRINT",FACE,{"disambiguationData":[TD([[makeQuery(id+"F2.imprint","IMPRINT",EDGE,{"derivedFrom":sQuery(id+"F2.wireOp",EDGE,"E2.5.3.0")}),-1.0]])]});
            var Q34;
            Q34=makeQuery(id+"F2.imprint","IMPRINT",FACE,{"disambiguationData":[TD([[makeQuery(id+"F2.imprint","IMPRINT",EDGE,{"derivedFrom":sQuery(id+"F2.wireOp",EDGE,"E2.17.7.0")}),-1.0]])]});
            var Q35;
            Q35=makeQuery(id+"F2.imprint","IMPRINT",FACE,{"disambiguationData":[TD([[makeQuery(id+"F2.imprint","IMPRINT",EDGE,{"derivedFrom":sQuery(id+"F2.wireOp",EDGE,"E2.16.0.0")}),-1.0]])]});
            var Q36;
            Q36=makeQuery(id+"F2.imprint","IMPRINT",FACE,{"disambiguationData":[TD([[makeQuery(id+"F2.imprint","IMPRINT",EDGE,{"derivedFrom":sQuery(id+"F2.wireOp",EDGE,"E2.14.2.0")}),-1.0]])]});
            var Q37;
            Q37=makeQuery(id+"F2.imprint","IMPRINT",FACE,{"disambiguationData":[TD([[makeQuery(id+"F2.imprint","IMPRINT",EDGE,{"derivedFrom":sQuery(id+"F2.wireOp",EDGE,"E2.12.4.0")}),-1.0]])]});
            var Q38;
            Q38=makeQuery(id+"F2.imprint","IMPRINT",FACE,{"disambiguationData":[TD([[makeQuery(id+"F2.imprint","IMPRINT",EDGE,{"derivedFrom":sQuery(id+"F2.wireOp",EDGE,"E2.3.6.0")}),-1.0]])]});
            var Q39;
            Q39=makeQuery(id+"F2.imprint","IMPRINT",FACE,{"disambiguationData":[TD([[makeQuery(id+"F2.imprint","IMPRINT",EDGE,{"derivedFrom":sQuery(id+"F2.wireOp",EDGE,"E2.1.8.0")}),-1.0]])]});
            var Q40;
            Q40=makeQuery(id+"F2.imprint","IMPRINT",FACE,{"disambiguationData":[TD([[makeQuery(id+"F2.imprint","IMPRINT",EDGE,{"derivedFrom":sQuery(id+"F2.wireOp",EDGE,"E2.10.7.0")}),-1.0]])]});
            var Q41;
            Q41=makeQuery(id+"F2.imprint","IMPRINT",FACE,{"disambiguationData":[TD([[makeQuery(id+"F2.imprint","IMPRINT",EDGE,{"derivedFrom":sQuery(id+"F2.wireOp",EDGE,"E2.9.0.0")}),-1.0]])]});
            var Q42;
            Q42=makeQuery(id+"F2.imprint","IMPRINT",FACE,{"disambiguationData":[TD([[makeQuery(id+"F2.imprint","IMPRINT",EDGE,{"derivedFrom":sQuery(id+"F2.wireOp",EDGE,"E2.7.2.0")}),-1.0]])]});
            var Q43;
            Q43=makeQuery(id+"F2.imprint","IMPRINT",FACE,{"disambiguationData":[TD([[makeQuery(id+"F2.imprint","IMPRINT",EDGE,{"derivedFrom":sQuery(id+"F2.wireOp",EDGE,"E2.5.4.0")}),-1.0]])]});
            var Q44;
            Q44=makeQuery(id+"F2.imprint","IMPRINT",FACE,{"disambiguationData":[TD([[makeQuery(id+"F2.imprint","IMPRINT",EDGE,{"derivedFrom":sQuery(id+"F2.wireOp",EDGE,"E2.17.8.0")}),-1.0]])]});
            var Q45;
            Q45=makeQuery(id+"F2.imprint","IMPRINT",FACE,{"disambiguationData":[TD([[makeQuery(id+"F2.imprint","IMPRINT",EDGE,{"derivedFrom":sQuery(id+"F2.wireOp",EDGE,"E2.16.1.0")}),-1.0]])]});
            var Q46;
            Q46=makeQuery(id+"F2.imprint","IMPRINT",FACE,{"disambiguationData":[TD([[makeQuery(id+"F2.imprint","IMPRINT",EDGE,{"derivedFrom":sQuery(id+"F2.wireOp",EDGE,"E2.14.3.0")}),-1.0]])]});
            var Q47;
            Q47=makeQuery(id+"F2.imprint","IMPRINT",FACE,{"disambiguationData":[TD([[makeQuery(id+"F2.imprint","IMPRINT",EDGE,{"derivedFrom":sQuery(id+"F2.wireOp",EDGE,"E2.12.5.0")}),-1.0]])]});
            var Q48;
            Q48=makeQuery(id+"F2.imprint","IMPRINT",FACE,{"disambiguationData":[TD([[makeQuery(id+"F2.imprint","IMPRINT",EDGE,{"derivedFrom":sQuery(id+"F2.wireOp",EDGE,"E2.3.7.0")}),-1.0]])]});
            var Q49;
            Q49=makeQuery(id+"F2.imprint","IMPRINT",FACE,{"disambiguationData":[TD([[makeQuery(id+"F2.imprint","IMPRINT",EDGE,{"derivedFrom":sQuery(id+"F2.wireOp",EDGE,"E2.2.0.0")}),-1.0]])]});
            var Q50;
            Q50=makeQuery(id+"F2.imprint","IMPRINT",FACE,{"disambiguationData":[TD([[makeQuery(id+"F2.imprint","IMPRINT",EDGE,{"derivedFrom":sQuery(id+"F2.wireOp",EDGE,"E2.10.8.0")}),-1.0]])]});
            var Q51;
            Q51=makeQuery(id+"F2.imprint","IMPRINT",FACE,{"disambiguationData":[TD([[makeQuery(id+"F2.imprint","IMPRINT",EDGE,{"derivedFrom":sQuery(id+"F2.wireOp",EDGE,"E2.9.1.0")}),-1.0]])]});
            var Q52;
            Q52=makeQuery(id+"F2.imprint","IMPRINT",FACE,{"disambiguationData":[TD([[makeQuery(id+"F2.imprint","IMPRINT",EDGE,{"derivedFrom":sQuery(id+"F2.wireOp",EDGE,"E2.7.3.0")}),-1.0]])]});
            var Q53;
            Q53=makeQuery(id+"F2.imprint","IMPRINT",FACE,{"disambiguationData":[TD([[makeQuery(id+"F2.imprint","IMPRINT",EDGE,{"derivedFrom":sQuery(id+"F2.wireOp",EDGE,"E2.5.5.0")}),-1.0]])]});
            var Q54;
            Q54=makeQuery(id+"F2.imprint","IMPRINT",FACE,{"disambiguationData":[TD([[makeQuery(id+"F2.imprint","IMPRINT",EDGE,{"derivedFrom":sQuery(id+"F2.wireOp",EDGE,"E2.18.0.0")}),-1.0]])]});
            var Q55;
            Q55=makeQuery(id+"F2.imprint","IMPRINT",FACE,{"disambiguationData":[TD([[makeQuery(id+"F2.imprint","IMPRINT",EDGE,{"derivedFrom":sQuery(id+"F2.wireOp",EDGE,"E2.16.2.0")}),-1.0]])]});
            var Q56;
            Q56=makeQuery(id+"F2.imprint","IMPRINT",FACE,{"disambiguationData":[TD([[makeQuery(id+"F2.imprint","IMPRINT",EDGE,{"derivedFrom":sQuery(id+"F2.wireOp",EDGE,"E2.14.4.0")}),-1.0]])]});
            var Q57;
            Q57=makeQuery(id+"F2.imprint","IMPRINT",FACE,{"disambiguationData":[TD([[makeQuery(id+"F2.imprint","IMPRINT",EDGE,{"derivedFrom":sQuery(id+"F2.wireOp",EDGE,"E2.12.6.0")}),-1.0]])]});
            var Q58;
            Q58=makeQuery(id+"F2.imprint","IMPRINT",FACE,{"disambiguationData":[TD([[makeQuery(id+"F2.imprint","IMPRINT",EDGE,{"derivedFrom":sQuery(id+"F2.wireOp",EDGE,"E2.3.8.0")}),-1.0]])]});
            var Q59;
            Q59=makeQuery(id+"F2.imprint","IMPRINT",FACE,{"disambiguationData":[TD([[makeQuery(id+"F2.imprint","IMPRINT",EDGE,{"derivedFrom":sQuery(id+"F2.wireOp",EDGE,"E2.2.1.0")}),-1.0]])]});
            var Q60;
            Q60=makeQuery(id+"F2.imprint","IMPRINT",FACE,{"disambiguationData":[TD([[makeQuery(id+"F2.imprint","IMPRINT",EDGE,{"derivedFrom":sQuery(id+"F2.wireOp",EDGE,"E2.11.0.0")}),-1.0]])]});
            var Q61;
            Q61=makeQuery(id+"F2.imprint","IMPRINT",FACE,{"disambiguationData":[TD([[makeQuery(id+"F2.imprint","IMPRINT",EDGE,{"derivedFrom":sQuery(id+"F2.wireOp",EDGE,"E2.9.2.0")}),-1.0]])]});
            var Q62;
            Q62=makeQuery(id+"F2.imprint","IMPRINT",FACE,{"disambiguationData":[TD([[makeQuery(id+"F2.imprint","IMPRINT",EDGE,{"derivedFrom":sQuery(id+"F2.wireOp",EDGE,"E2.7.4.0")}),-1.0]])]});
            var Q63;
            Q63=makeQuery(id+"F2.imprint","IMPRINT",FACE,{"disambiguationData":[TD([[makeQuery(id+"F2.imprint","IMPRINT",EDGE,{"derivedFrom":sQuery(id+"F2.wireOp",EDGE,"E2.5.6.0")}),-1.0]])]});
            var Q64;
            Q64=makeQuery(id+"F2.imprint","IMPRINT",FACE,{"disambiguationData":[TD([[makeQuery(id+"F2.imprint","IMPRINT",EDGE,{"derivedFrom":sQuery(id+"F2.wireOp",EDGE,"E2.18.1.0")}),-1.0]])]});
            var Q65;
            Q65=makeQuery(id+"F2.imprint","IMPRINT",FACE,{"disambiguationData":[TD([[makeQuery(id+"F2.imprint","IMPRINT",EDGE,{"derivedFrom":sQuery(id+"F2.wireOp",EDGE,"E2.16.3.0")}),-1.0]])]});
            var Q66;
            Q66=makeQuery(id+"F2.imprint","IMPRINT",FACE,{"disambiguationData":[TD([[makeQuery(id+"F2.imprint","IMPRINT",EDGE,{"derivedFrom":sQuery(id+"F2.wireOp",EDGE,"E2.14.5.0")}),-1.0]])]});
            var Q67;
            Q67=makeQuery(id+"F2.imprint","IMPRINT",FACE,{"disambiguationData":[TD([[makeQuery(id+"F2.imprint","IMPRINT",EDGE,{"derivedFrom":sQuery(id+"F2.wireOp",EDGE,"E2.12.7.0")}),-1.0]])]});
            var Q68;
            Q68=makeQuery(id+"F2.imprint","IMPRINT",FACE,{"disambiguationData":[TD([[makeQuery(id+"F2.imprint","IMPRINT",EDGE,{"derivedFrom":sQuery(id+"F2.wireOp",EDGE,"E2.4.0.0")}),-1.0]])]});
            var Q69;
            Q69=makeQuery(id+"F2.imprint","IMPRINT",FACE,{"disambiguationData":[TD([[makeQuery(id+"F2.imprint","IMPRINT",EDGE,{"derivedFrom":sQuery(id+"F2.wireOp",EDGE,"E2.2.2.0")}),-1.0]])]});
            var Q70;
            Q70=makeQuery(id+"F2.imprint","IMPRINT",FACE,{"disambiguationData":[TD([[makeQuery(id+"F2.imprint","IMPRINT",EDGE,{"derivedFrom":sQuery(id+"F2.wireOp",EDGE,"E2.11.1.0")}),-1.0]])]});
            var Q71;
            Q71=makeQuery(id+"F2.imprint","IMPRINT",FACE,{"disambiguationData":[TD([[makeQuery(id+"F2.imprint","IMPRINT",EDGE,{"derivedFrom":sQuery(id+"F2.wireOp",EDGE,"E2.9.3.0")}),-1.0]])]});
            var Q72;
            Q72=makeQuery(id+"F2.imprint","IMPRINT",FACE,{"disambiguationData":[TD([[makeQuery(id+"F2.imprint","IMPRINT",EDGE,{"derivedFrom":sQuery(id+"F2.wireOp",EDGE,"E2.7.5.0")}),-1.0]])]});
            var Q73;
            Q73=makeQuery(id+"F2.imprint","IMPRINT",FACE,{"disambiguationData":[TD([[makeQuery(id+"F2.imprint","IMPRINT",EDGE,{"derivedFrom":sQuery(id+"F2.wireOp",EDGE,"E2.5.7.0")}),-1.0]])]});
            var Q74;
            Q74=makeQuery(id+"F2.imprint","IMPRINT",FACE,{"disambiguationData":[TD([[makeQuery(id+"F2.imprint","IMPRINT",EDGE,{"derivedFrom":sQuery(id+"F2.wireOp",EDGE,"E2.18.2.0")}),-1.0]])]});
            var Q75;
            Q75=makeQuery(id+"F2.imprint","IMPRINT",FACE,{"disambiguationData":[TD([[makeQuery(id+"F2.imprint","IMPRINT",EDGE,{"derivedFrom":sQuery(id+"F2.wireOp",EDGE,"E2.16.4.0")}),-1.0]])]});
            var Q76;
            Q76=makeQuery(id+"F2.imprint","IMPRINT",FACE,{"disambiguationData":[TD([[makeQuery(id+"F2.imprint","IMPRINT",EDGE,{"derivedFrom":sQuery(id+"F2.wireOp",EDGE,"E2.14.6.0")}),-1.0]])]});
            var Q77;
            Q77=makeQuery(id+"F2.imprint","IMPRINT",FACE,{"disambiguationData":[TD([[makeQuery(id+"F2.imprint","IMPRINT",EDGE,{"derivedFrom":sQuery(id+"F2.wireOp",EDGE,"E2.12.8.0")}),-1.0]])]});
            var Q78;
            Q78=makeQuery(id+"F2.imprint","IMPRINT",FACE,{"disambiguationData":[TD([[makeQuery(id+"F2.imprint","IMPRINT",EDGE,{"derivedFrom":sQuery(id+"F2.wireOp",EDGE,"E2.4.1.0")}),-1.0]])]});
            var Q79;
            Q79=makeQuery(id+"F2.imprint","IMPRINT",FACE,{"disambiguationData":[TD([[makeQuery(id+"F2.imprint","IMPRINT",EDGE,{"derivedFrom":sQuery(id+"F2.wireOp",EDGE,"E2.2.3.0")}),-1.0]])]});
            var Q80;
            Q80=makeQuery(id+"F2.imprint","IMPRINT",FACE,{"disambiguationData":[TD([[makeQuery(id+"F2.imprint","IMPRINT",EDGE,{"derivedFrom":sQuery(id+"F2.wireOp",EDGE,"E2.11.2.0")}),-1.0]])]});
            var Q81;
            Q81=makeQuery(id+"F2.imprint","IMPRINT",FACE,{"disambiguationData":[TD([[makeQuery(id+"F2.imprint","IMPRINT",EDGE,{"derivedFrom":sQuery(id+"F2.wireOp",EDGE,"E2.9.4.0")}),-1.0]])]});
            var Q82;
            Q82=makeQuery(id+"F2.imprint","IMPRINT",FACE,{"disambiguationData":[TD([[makeQuery(id+"F2.imprint","IMPRINT",EDGE,{"derivedFrom":sQuery(id+"F2.wireOp",EDGE,"E2.7.6.0")}),-1.0]])]});
            var Q83;
            Q83=makeQuery(id+"F2.imprint","IMPRINT",FACE,{"disambiguationData":[TD([[makeQuery(id+"F2.imprint","IMPRINT",EDGE,{"derivedFrom":sQuery(id+"F2.wireOp",EDGE,"E2.5.8.0")}),-1.0]])]});
            var Q84;
            Q84=makeQuery(id+"F2.imprint","IMPRINT",FACE,{"disambiguationData":[TD([[makeQuery(id+"F2.imprint","IMPRINT",EDGE,{"derivedFrom":sQuery(id+"F2.wireOp",EDGE,"E2.18.3.0")}),-1.0]])]});
            var Q85;
            Q85=makeQuery(id+"F2.imprint","IMPRINT",FACE,{"disambiguationData":[TD([[makeQuery(id+"F2.imprint","IMPRINT",EDGE,{"derivedFrom":sQuery(id+"F2.wireOp",EDGE,"E2.16.5.0")}),-1.0]])]});
            var Q86;
            Q86=makeQuery(id+"F2.imprint","IMPRINT",FACE,{"disambiguationData":[TD([[makeQuery(id+"F2.imprint","IMPRINT",EDGE,{"derivedFrom":sQuery(id+"F2.wireOp",EDGE,"E2.14.7.0")}),-1.0]])]});
            var Q87;
            Q87=makeQuery(id+"F2.imprint","IMPRINT",FACE,{"disambiguationData":[TD([[makeQuery(id+"F2.imprint","IMPRINT",EDGE,{"derivedFrom":sQuery(id+"F2.wireOp",EDGE,"E2.13.0.0")}),-1.0]])]});
            var Q88;
            Q88=makeQuery(id+"F2.imprint","IMPRINT",FACE,{"disambiguationData":[TD([[makeQuery(id+"F2.imprint","IMPRINT",EDGE,{"derivedFrom":sQuery(id+"F2.wireOp",EDGE,"E2.7.7.0")}),-1.0]])]});
            var Q89;
            Q89=makeQuery(id+"F2.imprint","IMPRINT",FACE,{"disambiguationData":[TD([[makeQuery(id+"F2.imprint","IMPRINT",EDGE,{"derivedFrom":sQuery(id+"F2.wireOp",EDGE,"E2.6.0.0")}),-1.0]])]});
            var Q90;
            Q90=makeQuery(id+"F2.imprint","IMPRINT",FACE,{"disambiguationData":[TD([[makeQuery(id+"F2.imprint","IMPRINT",EDGE,{"derivedFrom":sQuery(id+"F2.wireOp",EDGE,"E2.4.2.0")}),-1.0]])]});
            var Q91;
            Q91=makeQuery(id+"F2.imprint","IMPRINT",FACE,{"disambiguationData":[TD([[makeQuery(id+"F2.imprint","IMPRINT",EDGE,{"derivedFrom":sQuery(id+"F2.wireOp",EDGE,"E2.2.4.0")}),-1.0]])]});
            var Q92;
            Q92=makeQuery(id+"F2.imprint","IMPRINT",FACE,{"disambiguationData":[TD([[makeQuery(id+"F2.imprint","IMPRINT",EDGE,{"derivedFrom":sQuery(id+"F2.wireOp",EDGE,"E2.14.8.0")}),-1.0]])]});
            var Q93;
            Q93=makeQuery(id+"F2.imprint","IMPRINT",FACE,{"disambiguationData":[TD([[makeQuery(id+"F2.imprint","IMPRINT",EDGE,{"derivedFrom":sQuery(id+"F2.wireOp",EDGE,"E2.13.1.0")}),-1.0]])]});
            var Q94;
            Q94=makeQuery(id+"F2.imprint","IMPRINT",FACE,{"disambiguationData":[TD([[makeQuery(id+"F2.imprint","IMPRINT",EDGE,{"derivedFrom":sQuery(id+"F2.wireOp",EDGE,"E2.11.3.0")}),-1.0]])]});
            var Q95;
            Q95=makeQuery(id+"F2.imprint","IMPRINT",FACE,{"disambiguationData":[TD([[makeQuery(id+"F2.imprint","IMPRINT",EDGE,{"derivedFrom":sQuery(id+"F2.wireOp",EDGE,"E2.9.5.0")}),-1.0]])]});
            var Q96;
            Q96=makeQuery(id+"F2.imprint","IMPRINT",FACE,{"disambiguationData":[TD([[makeQuery(id+"F2.imprint","IMPRINT",EDGE,{"derivedFrom":sQuery(id+"F2.wireOp",EDGE,"E2.18.4.0")}),-1.0]])]});
            var Q97;
            Q97=makeQuery(id+"F2.imprint","IMPRINT",FACE,{"disambiguationData":[TD([[makeQuery(id+"F2.imprint","IMPRINT",EDGE,{"derivedFrom":sQuery(id+"F2.wireOp",EDGE,"E2.16.6.0")}),-1.0]])]});
            var Q98;
            Q98=makeQuery(id+"F2.imprint","IMPRINT",FACE,{"disambiguationData":[TD([[makeQuery(id+"F2.imprint","IMPRINT",EDGE,{"derivedFrom":sQuery(id+"F2.wireOp",EDGE,"E2.15.0.0")}),-1.0]])]});
            var Q99;
            Q99=makeQuery(id+"F2.imprint","IMPRINT",FACE,{"disambiguationData":[TD([[makeQuery(id+"F2.imprint","IMPRINT",EDGE,{"derivedFrom":sQuery(id+"F2.wireOp",EDGE,"E2.13.2.0")}),-1.0]])]});
            var Q100;
            Q100=makeQuery(id+"F2.imprint","IMPRINT",FACE,{"disambiguationData":[TD([[makeQuery(id+"F2.imprint","IMPRINT",EDGE,{"derivedFrom":sQuery(id+"F2.wireOp",EDGE,"E2.11.4.0")}),-1.0]])]});
            var Q101;
            Q101=makeQuery(id+"F2.imprint","IMPRINT",FACE,{"disambiguationData":[TD([[makeQuery(id+"F2.imprint","IMPRINT",EDGE,{"derivedFrom":sQuery(id+"F2.wireOp",EDGE,"E2.9.6.0")}),-1.0]])]});
            var Q102;
            Q102=makeQuery(id+"F2.imprint","IMPRINT",FACE,{"disambiguationData":[TD([[makeQuery(id+"F2.imprint","IMPRINT",EDGE,{"derivedFrom":sQuery(id+"F2.wireOp",EDGE,"E2.18.5.0")}),-1.0]])]});
            var Q103;
            Q103=makeQuery(id+"F2.imprint","IMPRINT",FACE,{"disambiguationData":[TD([[makeQuery(id+"F2.imprint","IMPRINT",EDGE,{"derivedFrom":sQuery(id+"F2.wireOp",EDGE,"E2.16.7.0")}),-1.0]])]});
            var Q104;
            Q104=makeQuery(id+"F2.imprint","IMPRINT",FACE,{"disambiguationData":[TD([[makeQuery(id+"F2.imprint","IMPRINT",EDGE,{"derivedFrom":sQuery(id+"F2.wireOp",EDGE,"E2.7.8.0")}),-1.0]])]});
            var Q105;
            Q105=makeQuery(id+"F2.imprint","IMPRINT",FACE,{"disambiguationData":[TD([[makeQuery(id+"F2.imprint","IMPRINT",EDGE,{"derivedFrom":sQuery(id+"F2.wireOp",EDGE,"E2.6.1.0")}),-1.0]])]});
            var Q106;
            Q106=makeQuery(id+"F2.imprint","IMPRINT",FACE,{"disambiguationData":[TD([[makeQuery(id+"F2.imprint","IMPRINT",EDGE,{"derivedFrom":sQuery(id+"F2.wireOp",EDGE,"E2.4.3.0")}),-1.0]])]});
            var Q107;
            Q107=makeQuery(id+"F2.imprint","IMPRINT",FACE,{"disambiguationData":[TD([[makeQuery(id+"F2.imprint","IMPRINT",EDGE,{"derivedFrom":sQuery(id+"F2.wireOp",EDGE,"E2.2.5.0")}),-1.0]])]});
            var Q108;
            Q108=makeQuery(id+"F2.imprint","IMPRINT",FACE,{"disambiguationData":[TD([[makeQuery(id+"F2.imprint","IMPRINT",EDGE,{"derivedFrom":sQuery(id+"F2.wireOp",EDGE,"E2.18.6.0")}),-1.0]])]});
            var Q109;
            Q109=makeQuery(id+"F2.imprint","IMPRINT",FACE,{"disambiguationData":[TD([[makeQuery(id+"F2.imprint","IMPRINT",EDGE,{"derivedFrom":sQuery(id+"F2.wireOp",EDGE,"E2.16.8.0")}),-1.0]])]});
            var Q110;
            Q110=makeQuery(id+"F2.imprint","IMPRINT",FACE,{"disambiguationData":[TD([[makeQuery(id+"F2.imprint","IMPRINT",EDGE,{"derivedFrom":sQuery(id+"F2.wireOp",EDGE,"E2.8.0.0")}),-1.0]])]});
            var Q111;
            Q111=makeQuery(id+"F2.imprint","IMPRINT",FACE,{"disambiguationData":[TD([[makeQuery(id+"F2.imprint","IMPRINT",EDGE,{"derivedFrom":sQuery(id+"F2.wireOp",EDGE,"E2.6.2.0")}),-1.0]])]});
            var Q112;
            Q112=makeQuery(id+"F2.imprint","IMPRINT",FACE,{"disambiguationData":[TD([[makeQuery(id+"F2.imprint","IMPRINT",EDGE,{"derivedFrom":sQuery(id+"F2.wireOp",EDGE,"E2.4.4.0")}),-1.0]])]});
            var Q113;
            Q113=makeQuery(id+"F2.imprint","IMPRINT",FACE,{"disambiguationData":[TD([[makeQuery(id+"F2.imprint","IMPRINT",EDGE,{"derivedFrom":sQuery(id+"F2.wireOp",EDGE,"E2.2.6.0")}),-1.0]])]});
            var Q114;
            Q114=makeQuery(id+"F2.imprint","IMPRINT",FACE,{"disambiguationData":[TD([[makeQuery(id+"F2.imprint","IMPRINT",EDGE,{"derivedFrom":sQuery(id+"F2.wireOp",EDGE,"E2.15.1.0")}),-1.0]])]});
            var Q115;
            Q115=makeQuery(id+"F2.imprint","IMPRINT",FACE,{"disambiguationData":[TD([[makeQuery(id+"F2.imprint","IMPRINT",EDGE,{"derivedFrom":sQuery(id+"F2.wireOp",EDGE,"E2.13.3.0")}),-1.0]])]});
            var Q116;
            Q116=makeQuery(id+"F2.imprint","IMPRINT",FACE,{"disambiguationData":[TD([[makeQuery(id+"F2.imprint","IMPRINT",EDGE,{"derivedFrom":sQuery(id+"F2.wireOp",EDGE,"E2.11.5.0")}),-1.0]])]});
            var Q117;
            Q117=makeQuery(id+"F2.imprint","IMPRINT",FACE,{"disambiguationData":[TD([[makeQuery(id+"F2.imprint","IMPRINT",EDGE,{"derivedFrom":sQuery(id+"F2.wireOp",EDGE,"E2.9.7.0")}),-1.0]])]});
            var Q118;
            Q118=makeQuery(id+"F2.imprint","IMPRINT",FACE,{"disambiguationData":[TD([[makeQuery(id+"F2.imprint","IMPRINT",EDGE,{"derivedFrom":sQuery(id+"F2.wireOp",EDGE,"E2.8.1.0")}),-1.0]])]});
            var Q119;
            Q119=makeQuery(id+"F2.imprint","IMPRINT",FACE,{"disambiguationData":[TD([[makeQuery(id+"F2.imprint","IMPRINT",EDGE,{"derivedFrom":sQuery(id+"F2.wireOp",EDGE,"E2.6.3.0")}),-1.0]])]});
            var Q120;
            Q120=makeQuery(id+"F2.imprint","IMPRINT",FACE,{"disambiguationData":[TD([[makeQuery(id+"F2.imprint","IMPRINT",EDGE,{"derivedFrom":sQuery(id+"F2.wireOp",EDGE,"E2.4.5.0")}),-1.0]])]});
            var Q121;
            Q121=makeQuery(id+"F2.imprint","IMPRINT",FACE,{"disambiguationData":[TD([[makeQuery(id+"F2.imprint","IMPRINT",EDGE,{"derivedFrom":sQuery(id+"F2.wireOp",EDGE,"E2.2.7.0")}),-1.0]])]});
            var Q122;
            Q122=makeQuery(id+"F2.imprint","IMPRINT",FACE,{"disambiguationData":[TD([[makeQuery(id+"F2.imprint","IMPRINT",EDGE,{"derivedFrom":sQuery(id+"F2.wireOp",EDGE,"E2.15.2.0")}),-1.0]])]});
            var Q123;
            Q123=makeQuery(id+"F2.imprint","IMPRINT",FACE,{"disambiguationData":[TD([[makeQuery(id+"F2.imprint","IMPRINT",EDGE,{"derivedFrom":sQuery(id+"F2.wireOp",EDGE,"E2.13.4.0")}),-1.0]])]});
            var Q124;
            Q124=makeQuery(id+"F2.imprint","IMPRINT",FACE,{"disambiguationData":[TD([[makeQuery(id+"F2.imprint","IMPRINT",EDGE,{"derivedFrom":sQuery(id+"F2.wireOp",EDGE,"E2.11.6.0")}),-1.0]])]});
            var Q125;
            Q125=makeQuery(id+"F2.imprint","IMPRINT",FACE,{"disambiguationData":[TD([[makeQuery(id+"F2.imprint","IMPRINT",EDGE,{"derivedFrom":sQuery(id+"F2.wireOp",EDGE,"E2.9.8.0")}),-1.0]])]});
            var Q126;
            Q126=makeQuery(id+"F2.imprint","IMPRINT",FACE,{"disambiguationData":[TD([[makeQuery(id+"F2.imprint","IMPRINT",EDGE,{"derivedFrom":sQuery(id+"F2.wireOp",EDGE,"E2.18.7.0")}),-1.0]])]});
            var Q127;
            Q127=makeQuery(id+"F2.imprint","IMPRINT",FACE,{"disambiguationData":[TD([[makeQuery(id+"F2.imprint","IMPRINT",EDGE,{"derivedFrom":sQuery(id+"F2.wireOp",EDGE,"E2.17.0.0")}),-1.0]])]});
            var Q128;
            Q128=makeQuery(id+"F2.imprint","IMPRINT",FACE,{"disambiguationData":[TD([[makeQuery(id+"F2.imprint","IMPRINT",EDGE,{"derivedFrom":sQuery(id+"F2.wireOp",EDGE,"E2.8.2.0")}),-1.0]])]});
            var Q129;
            Q129=makeQuery(id+"F2.imprint","IMPRINT",FACE,{"disambiguationData":[TD([[makeQuery(id+"F2.imprint","IMPRINT",EDGE,{"derivedFrom":sQuery(id+"F2.wireOp",EDGE,"E2.6.4.0")}),-1.0]])]});
            var Q130;
            Q130=makeQuery(id+"F2.imprint","IMPRINT",FACE,{"disambiguationData":[TD([[makeQuery(id+"F2.imprint","IMPRINT",EDGE,{"derivedFrom":sQuery(id+"F2.wireOp",EDGE,"E2.4.6.0")}),-1.0]])]});
            var Q131;
            Q131=makeQuery(id+"F2.imprint","IMPRINT",FACE,{"disambiguationData":[TD([[makeQuery(id+"F2.imprint","IMPRINT",EDGE,{"derivedFrom":sQuery(id+"F2.wireOp",EDGE,"E2.2.8.0")}),-1.0]])]});
            var Q132;
            Q132=makeQuery(id+"F2.imprint","IMPRINT",FACE,{"disambiguationData":[TD([[makeQuery(id+"F2.imprint","IMPRINT",EDGE,{"derivedFrom":sQuery(id+"F2.wireOp",EDGE,"E2.15.3.0")}),-1.0]])]});
            var Q133;
            Q133=makeQuery(id+"F2.imprint","IMPRINT",FACE,{"disambiguationData":[TD([[makeQuery(id+"F2.imprint","IMPRINT",EDGE,{"derivedFrom":sQuery(id+"F2.wireOp",EDGE,"E2.13.5.0")}),-1.0]])]});
            var Q134;
            Q134=makeQuery(id+"F2.imprint","IMPRINT",FACE,{"disambiguationData":[TD([[makeQuery(id+"F2.imprint","IMPRINT",EDGE,{"derivedFrom":sQuery(id+"F2.wireOp",EDGE,"E2.11.7.0")}),-1.0]])]});
            var Q135;
            Q135=makeQuery(id+"F2.imprint","IMPRINT",FACE,{"disambiguationData":[TD([[makeQuery(id+"F2.imprint","IMPRINT",EDGE,{"derivedFrom":sQuery(id+"F2.wireOp",EDGE,"E2.10.0.0")}),-1.0]])]});
            var Q136;
            Q136=makeQuery(id+"F2.imprint","IMPRINT",FACE,{"disambiguationData":[TD([[makeQuery(id+"F2.imprint","IMPRINT",EDGE,{"derivedFrom":sQuery(id+"F2.wireOp",EDGE,"E2.18.8.0")}),-1.0]])]});
            var Q137;
            Q137=makeQuery(id+"F2.imprint","IMPRINT",FACE,{"disambiguationData":[TD([[makeQuery(id+"F2.imprint","IMPRINT",EDGE,{"derivedFrom":sQuery(id+"F2.wireOp",EDGE,"E2.17.1.0")}),-1.0]])]});
            var Q138;
            Q138=makeQuery(id+"F2.imprint","IMPRINT",FACE,{"disambiguationData":[TD([[makeQuery(id+"F2.imprint","IMPRINT",EDGE,{"derivedFrom":sQuery(id+"F2.wireOp",EDGE,"E2.8.3.0")}),-1.0]])]});
            var Q139;
            Q139=makeQuery(id+"F2.imprint","IMPRINT",FACE,{"disambiguationData":[TD([[makeQuery(id+"F2.imprint","IMPRINT",EDGE,{"derivedFrom":sQuery(id+"F2.wireOp",EDGE,"E2.6.5.0")}),-1.0]])]});
            var Q140;
            Q140=makeQuery(id+"F2.imprint","IMPRINT",FACE,{"disambiguationData":[TD([[makeQuery(id+"F2.imprint","IMPRINT",EDGE,{"derivedFrom":sQuery(id+"F2.wireOp",EDGE,"E2.4.7.0")}),-1.0]])]});
            var Q141;
            Q141=makeQuery(id+"F2.imprint","IMPRINT",FACE,{"disambiguationData":[TD([[makeQuery(id+"F2.imprint","IMPRINT",EDGE,{"derivedFrom":sQuery(id+"F2.wireOp",EDGE,"E2.3.0.0")}),-1.0]])]});
            var Q142;
            Q142=makeQuery(id+"F2.imprint","IMPRINT",FACE,{"disambiguationData":[TD([[makeQuery(id+"F2.imprint","IMPRINT",EDGE,{"derivedFrom":sQuery(id+"F2.wireOp",EDGE,"E2.15.4.0")}),-1.0]])]});
            var Q143;
            Q143=makeQuery(id+"F2.imprint","IMPRINT",FACE,{"disambiguationData":[TD([[makeQuery(id+"F2.imprint","IMPRINT",EDGE,{"derivedFrom":sQuery(id+"F2.wireOp",EDGE,"E2.13.6.0")}),-1.0]])]});
            var Q144;
            Q144=makeQuery(id+"F2.imprint","IMPRINT",FACE,{"disambiguationData":[TD([[makeQuery(id+"F2.imprint","IMPRINT",EDGE,{"derivedFrom":sQuery(id+"F2.wireOp",EDGE,"E2.11.8.0")}),-1.0]])]});
            var Q145;
            Q145=makeQuery(id+"F2.imprint","IMPRINT",FACE,{"disambiguationData":[TD([[makeQuery(id+"F2.imprint","IMPRINT",EDGE,{"derivedFrom":sQuery(id+"F2.wireOp",EDGE,"E2.10.1.0")}),-1.0]])]});
            var Q146;
            Q146=makeQuery(id+"F2.imprint","IMPRINT",FACE,{"disambiguationData":[TD([[makeQuery(id+"F2.imprint","IMPRINT",EDGE,{"derivedFrom":sQuery(id+"F2.wireOp",EDGE,"E2.17.2.0")}),-1.0]])]});
            var Q147;
            Q147=makeQuery(id+"F2.imprint","IMPRINT",FACE,{"disambiguationData":[TD([[makeQuery(id+"F2.imprint","IMPRINT",EDGE,{"derivedFrom":sQuery(id+"F2.wireOp",EDGE,"E2.8.4.0")}),-1.0]])]});
            var Q148;
            Q148=makeQuery(id+"F2.imprint","IMPRINT",FACE,{"disambiguationData":[TD([[makeQuery(id+"F2.imprint","IMPRINT",EDGE,{"derivedFrom":sQuery(id+"F2.wireOp",EDGE,"E2.6.6.0")}),-1.0]])]});
            var Q149;
            Q149=makeQuery(id+"F2.imprint","IMPRINT",FACE,{"disambiguationData":[TD([[makeQuery(id+"F2.imprint","IMPRINT",EDGE,{"derivedFrom":sQuery(id+"F2.wireOp",EDGE,"E2.4.8.0")}),-1.0]])]});
            var Q150;
            Q150=makeQuery(id+"F2.imprint","IMPRINT",FACE,{"disambiguationData":[TD([[makeQuery(id+"F2.imprint","IMPRINT",EDGE,{"derivedFrom":sQuery(id+"F2.wireOp",EDGE,"E2.3.1.0")}),-1.0]])]});
            var Q151;
            Q151=makeQuery(id+"F2.imprint","IMPRINT",FACE,{"disambiguationData":[TD([[makeQuery(id+"F2.imprint","IMPRINT",EDGE,{"derivedFrom":sQuery(id+"F2.wireOp",EDGE,"E2.15.5.0")}),-1.0]])]});
            var Q152;
            Q152=makeQuery(id+"F2.imprint","IMPRINT",FACE,{"disambiguationData":[TD([[makeQuery(id+"F2.imprint","IMPRINT",EDGE,{"derivedFrom":sQuery(id+"F2.wireOp",EDGE,"E2.13.7.0")}),-1.0]])]});
            var Q153;
            Q153=makeQuery(id+"F2.imprint","IMPRINT",FACE,{"disambiguationData":[TD([[makeQuery(id+"F2.imprint","IMPRINT",EDGE,{"derivedFrom":sQuery(id+"F2.wireOp",EDGE,"E2.12.0.0")}),-1.0]])]});
            var Q154;
            Q154=makeQuery(id+"F2.imprint","IMPRINT",FACE,{"disambiguationData":[TD([[makeQuery(id+"F2.imprint","IMPRINT",EDGE,{"derivedFrom":sQuery(id+"F2.wireOp",EDGE,"E2.10.2.0")}),-1.0]])]});
            var Q155;
            Q155=makeQuery(id+"F2.imprint","IMPRINT",FACE,{"disambiguationData":[TD([[makeQuery(id+"F2.imprint","IMPRINT",EDGE,{"derivedFrom":sQuery(id+"F2.wireOp",EDGE,"E2.17.3.0")}),-1.0]])]});
            var Q156;
            Q156=makeQuery(id+"F2.imprint","IMPRINT",FACE,{"disambiguationData":[TD([[makeQuery(id+"F2.imprint","IMPRINT",EDGE,{"derivedFrom":sQuery(id+"F2.wireOp",EDGE,"E2.1.6.0")}),-1.0]])]});
            var Q157;
            Q157=makeQuery(id+"F2.imprint","IMPRINT",FACE,{"disambiguationData":[TD([[makeQuery(id+"F2.imprint","IMPRINT",EDGE,{"derivedFrom":sQuery(id+"F2.wireOp",EDGE,"E2.1.4.0")}),-1.0]])]});
            var Q158;
            Q158=makeQuery(id+"F2.imprint","IMPRINT",FACE,{"disambiguationData":[TD([[makeQuery(id+"F2.imprint","IMPRINT",EDGE,{"derivedFrom":sQuery(id+"F2.wireOp",EDGE,"E2.1.5.0")}),-1.0]])]});
            var Q159;
            Q159=makeQuery(id+"F2.imprint","IMPRINT",FACE,{"disambiguationData":[TD([[makeQuery(id+"F2.imprint","IMPRINT",EDGE,{"derivedFrom":sQuery(id+"F2.wireOp",EDGE,"E2.0.1.0")}),-1.0]])]});
            var Q160;
            Q160=makeQuery(id+"F2.imprint","IMPRINT",FACE,{"disambiguationData":[TD([[makeQuery(id+"F2.imprint","IMPRINT",EDGE,{"derivedFrom":sQuery(id+"F2.wireOp",EDGE,"E2.0.2.0")}),-1.0]])]});
            var Q161;
            Q161=makeQuery(id+"F2.imprint","IMPRINT",FACE,{"disambiguationData":[TD([[makeQuery(id+"F2.imprint","IMPRINT",EDGE,{"derivedFrom":sQuery(id+"F2.wireOp",EDGE,"E2.0.3.0")}),-1.0]])]});
            var Q162;
            Q162=makeQuery(id+"F2.imprint","IMPRINT",FACE,{"disambiguationData":[TD([[makeQuery(id+"F2.imprint","IMPRINT",EDGE,{"derivedFrom":sQuery(id+"F2.wireOp",EDGE,"E2.0.4.0")}),-1.0]])]});
            var Q163;
            Q163=makeQuery(id+"F2.imprint","IMPRINT",FACE,{"disambiguationData":[TD([[makeQuery(id+"F2.imprint","IMPRINT",EDGE,{"derivedFrom":sQuery(id+"F2.wireOp",EDGE,"E2.0.5.0")}),-1.0]])]});
            var Q164;
            Q164=makeQuery(id+"F2.imprint","IMPRINT",FACE,{"disambiguationData":[TD([[makeQuery(id+"F2.imprint","IMPRINT",EDGE,{"derivedFrom":sQuery(id+"F2.wireOp",EDGE,"E2.0.6.0")}),-1.0]])]});
            var Q165;
            Q165=makeQuery(id+"F2.imprint","IMPRINT",FACE,{"disambiguationData":[TD([[makeQuery(id+"F2.imprint","IMPRINT",EDGE,{"derivedFrom":sQuery(id+"F2.wireOp",EDGE,"E2.0.7.0")}),-1.0]])]});
            var Q166;
            Q166=makeQuery(id+"F2.imprint","IMPRINT",FACE,{"disambiguationData":[TD([[makeQuery(id+"F2.imprint","IMPRINT",EDGE,{"derivedFrom":sQuery(id+"F2.wireOp",EDGE,"E2.0.8.0")}),-1.0]])]});
            var Q167;
            Q167=makeQuery(id+"F2.imprint","IMPRINT",FACE,{"disambiguationData":[TD([[makeQuery(id+"F2.imprint","IMPRINT",EDGE,{"derivedFrom":sQuery(id+"F2.wireOp",EDGE,"E2.1.0.0")}),-1.0]])]});
            var Q168;
            Q168=makeQuery(id+"F2.imprint","IMPRINT",FACE,{"disambiguationData":[TD([[makeQuery(id+"F2.imprint","IMPRINT",EDGE,{"derivedFrom":sQuery(id+"F2.wireOp",EDGE,"E2.1.1.0")}),-1.0]])]});
            var Q169;
            Q169=makeQuery(id+"F2.imprint","IMPRINT",FACE,{"disambiguationData":[TD([[makeQuery(id+"F2.imprint","IMPRINT",EDGE,{"derivedFrom":sQuery(id+"F2.wireOp",EDGE,"E2.1.2.0")}),-1.0]])]});
            var Q170;
            Q170=makeQuery(id+"F2.imprint","IMPRINT",FACE,{"disambiguationData":[TD([[makeQuery(id+"F2.imprint","IMPRINT",EDGE,{"derivedFrom":sQuery(id+"F2.wireOp",EDGE,"E2.1.3.0")}),-1.0]])]});
            extrude(context, id + "F3", {"entities" : qUnion([Q0, Q1, Q2, Q3, Q4, Q5, Q6, Q7, Q8, Q9, Q10, Q11, Q12, Q13, Q14, Q15, Q16, Q17, Q18, Q19, Q20, Q21, Q22, Q23, Q24, Q25, Q26, Q27, Q28, Q29, Q30, Q31, Q32, Q33, Q34, Q35, Q36, Q37, Q38, Q39, Q40, Q41, Q42, Q43, Q44, Q45, Q46, Q47, Q48, Q49, Q50, Q51, Q52, Q53, Q54, Q55, Q56, Q57, Q58, Q59, Q60, Q61, Q62, Q63, Q64, Q65, Q66, Q67, Q68, Q69, Q70, Q71, Q72, Q73, Q74, Q75, Q76, Q77, Q78, Q79, Q80, Q81, Q82, Q83, Q84, Q85, Q86, Q87, Q88, Q89, Q90, Q91, Q92, Q93, Q94, Q95, Q96, Q97, Q98, Q99, Q100, Q101, Q102, Q103, Q104, Q105, Q106, Q107, Q108, Q109, Q110, Q111, Q112, Q113, Q114, Q115, Q116, Q117, Q118, Q119, Q120, Q121, Q122, Q123, Q124, Q125, Q126, Q127, Q128, Q129, Q130, Q131, Q132, Q133, Q134, Q135, Q136, Q137, Q138, Q139, Q140, Q141, Q142, Q143, Q144, Q145, Q146, Q147, Q148, Q149, Q150, Q151, Q152, Q153, Q154, Q155, Q156, Q157, Q158, Q159, Q160, Q161, Q162, Q163, Q164, Q165, Q166, Q167, Q168, Q169, Q170]), "operationType" : NewBodyOperationType.REMOVE, "oppositeDirection" : true, "depth" : 25 * mm, "offsetDistance" : 25 * mm});
        }
    });
